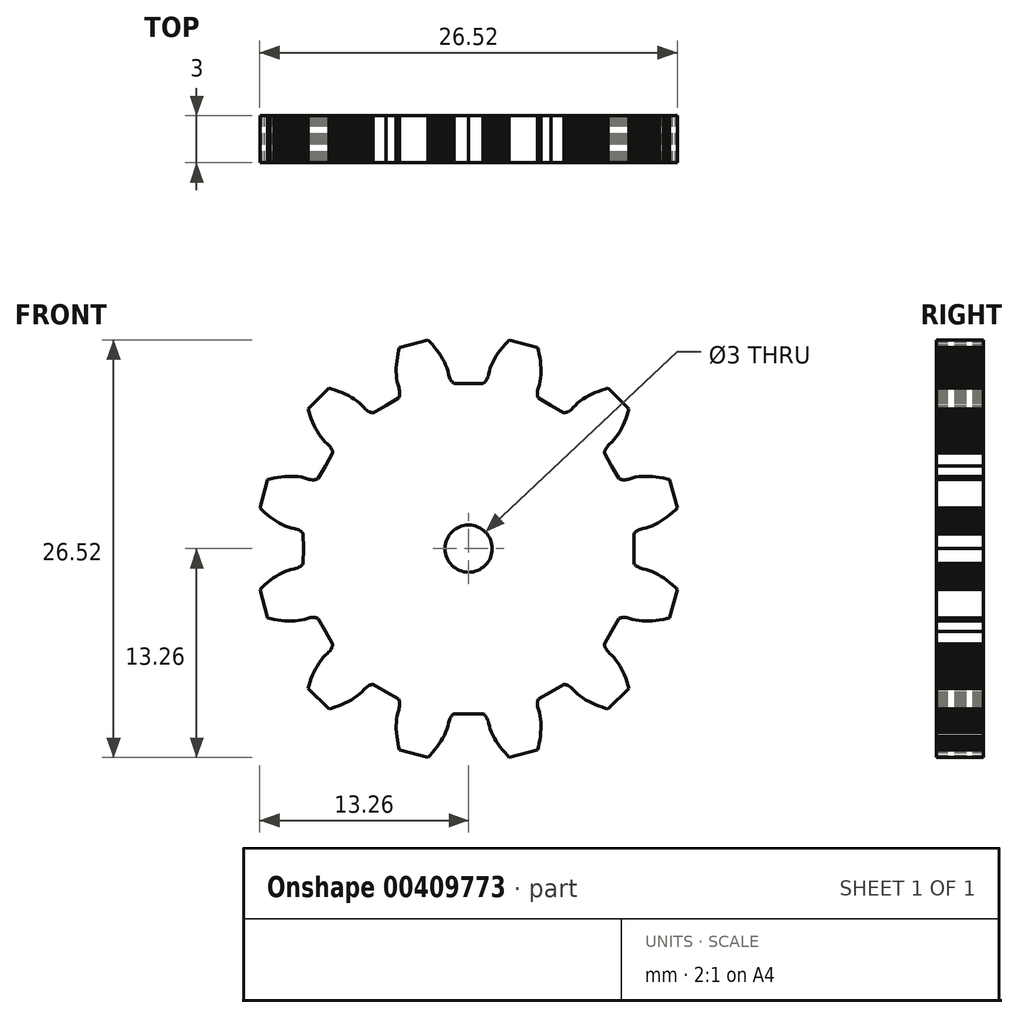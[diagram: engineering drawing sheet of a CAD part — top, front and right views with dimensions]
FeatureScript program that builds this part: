
annotation { "Feature Type Name" : "Feature", "Feature Type Description" : "" }
export const myFeature = defineFeature(function(context is Context, id is Id, definition is map)
    precondition{}
    {
        {
            var Q0;
            Q0=qCreatedBy(makeId("Front.planeOp"),FACE);
            var sketch = newSketch(context, id + "F0", { "sketchPlane" : qUnion([Q0])});
            skLineSegment(sketch, "E0", {"start": v(-10.5, 0) * mm, "end": v(-10.5, 0.93) * mm});
            skLineSegment(sketch, "E1", {"start": v(-10.5, 0.93) * mm, "end": v(-10.55, 1) * mm});
            skLineSegment(sketch, "E2", {"start": v(-10.55, 1) * mm, "end": v(-10.6, 1.05) * mm});
            skLineSegment(sketch, "E3", {"start": v(-10.6, 1.05) * mm, "end": v(-10.64, 1.09) * mm});
            skLineSegment(sketch, "E4", {"start": v(-10.64, 1.09) * mm, "end": v(-10.69, 1.12) * mm});
            skLineSegment(sketch, "E5", {"start": v(-10.69, 1.12) * mm, "end": v(-10.78, 1.17) * mm});
            skLineSegment(sketch, "E6", {"start": v(-10.78, 1.17) * mm, "end": v(-10.88, 1.22) * mm});
            skLineSegment(sketch, "E7", {"start": v(-10.88, 1.22) * mm, "end": v(-10.97, 1.25) * mm});
            skLineSegment(sketch, "E8", {"start": v(-10.97, 1.25) * mm, "end": v(-11.07, 1.28) * mm});
            skLineSegment(sketch, "E9", {"start": v(-11.07, 1.28) * mm, "end": v(-11.27, 1.32) * mm});
            skLineSegment(sketch, "E10", {"start": v(-11.27, 1.32) * mm, "end": v(-11.47, 1.38) * mm});
            skLineSegment(sketch, "E11", {"start": v(-11.47, 1.38) * mm, "end": v(-11.66, 1.45) * mm});
            skLineSegment(sketch, "E12", {"start": v(-11.66, 1.45) * mm, "end": v(-11.85, 1.54) * mm});
            skLineSegment(sketch, "E13", {"start": v(-11.85, 1.54) * mm, "end": v(-12.04, 1.64) * mm});
            skLineSegment(sketch, "E14", {"start": v(-12.04, 1.64) * mm, "end": v(-12.23, 1.76) * mm});
            skLineSegment(sketch, "E15", {"start": v(-12.23, 1.76) * mm, "end": v(-12.41, 1.88) * mm});
            skLineSegment(sketch, "E16", {"start": v(-12.41, 1.88) * mm, "end": v(-12.6, 2.01) * mm});
            skLineSegment(sketch, "E17", {"start": v(-12.6, 2.01) * mm, "end": v(-12.77, 2.15) * mm});
            skLineSegment(sketch, "E18", {"start": v(-12.77, 2.15) * mm, "end": v(-12.95, 2.3) * mm});
            skLineSegment(sketch, "E19", {"start": v(-12.95, 2.3) * mm, "end": v(-13.13, 2.46) * mm});
            skLineSegment(sketch, "E20", {"start": v(-13.13, 2.46) * mm, "end": v(-13.26, 2.58) * mm});
            skLineSegment(sketch, "E21", {"start": v(-13.26, 2.58) * mm, "end": v(-12.77, 4.4) * mm});
            skLineSegment(sketch, "E22", {"start": v(-12.77, 4.4) * mm, "end": v(-12.6, 4.43) * mm});
            skLineSegment(sketch, "E23", {"start": v(-12.6, 4.43) * mm, "end": v(-12.37, 4.48) * mm});
            skLineSegment(sketch, "E24", {"start": v(-12.37, 4.48) * mm, "end": v(-12.14, 4.52) * mm});
            skLineSegment(sketch, "E25", {"start": v(-12.14, 4.52) * mm, "end": v(-11.91, 4.56) * mm});
            skLineSegment(sketch, "E26", {"start": v(-11.91, 4.56) * mm, "end": v(-11.69, 4.58) * mm});
            skLineSegment(sketch, "E27", {"start": v(-11.69, 4.58) * mm, "end": v(-11.47, 4.6) * mm});
            skLineSegment(sketch, "E28", {"start": v(-11.47, 4.6) * mm, "end": v(-11.25, 4.6) * mm});
            skLineSegment(sketch, "E29", {"start": v(-11.25, 4.6) * mm, "end": v(-11.03, 4.59) * mm});
            skLineSegment(sketch, "E30", {"start": v(-11.03, 4.59) * mm, "end": v(-10.82, 4.57) * mm});
            skLineSegment(sketch, "E31", {"start": v(-10.82, 4.57) * mm, "end": v(-10.62, 4.54) * mm});
            skLineSegment(sketch, "E32", {"start": v(-10.62, 4.54) * mm, "end": v(-10.42, 4.5) * mm});
            skLineSegment(sketch, "E33", {"start": v(-10.42, 4.5) * mm, "end": v(-10.23, 4.43) * mm});
            skLineSegment(sketch, "E34", {"start": v(-10.23, 4.43) * mm, "end": v(-10.13, 4.4) * mm});
            skLineSegment(sketch, "E35", {"start": v(-10.13, 4.4) * mm, "end": v(-10.03, 4.38) * mm});
            skLineSegment(sketch, "E36", {"start": v(-10.03, 4.38) * mm, "end": v(-9.92, 4.37) * mm});
            skLineSegment(sketch, "E37", {"start": v(-9.92, 4.37) * mm, "end": v(-9.81, 4.37) * mm});
            skLineSegment(sketch, "E38", {"start": v(-9.81, 4.37) * mm, "end": v(-9.76, 4.38) * mm});
            skLineSegment(sketch, "E39", {"start": v(-9.76, 4.38) * mm, "end": v(-9.7, 4.39) * mm});
            skLineSegment(sketch, "E40", {"start": v(-9.7, 4.39) * mm, "end": v(-9.63, 4.4) * mm});
            skLineSegment(sketch, "E41", {"start": v(-9.63, 4.4) * mm, "end": v(-9.56, 4.44) * mm});
            skLineSegment(sketch, "E42", {"start": v(-9.56, 4.44) * mm, "end": v(-9.09, 5.25) * mm});
            skLineSegment(sketch, "E43", {"start": v(-9.09, 5.25) * mm, "end": v(-8.63, 6.06) * mm});
            skLineSegment(sketch, "E44", {"start": v(-8.63, 6.06) * mm, "end": v(-8.63, 6.14) * mm});
            skLineSegment(sketch, "E45", {"start": v(-8.63, 6.14) * mm, "end": v(-8.65, 6.2) * mm});
            skLineSegment(sketch, "E46", {"start": v(-8.65, 6.2) * mm, "end": v(-8.67, 6.26) * mm});
            skLineSegment(sketch, "E47", {"start": v(-8.67, 6.26) * mm, "end": v(-8.7, 6.31) * mm});
            skLineSegment(sketch, "E48", {"start": v(-8.7, 6.31) * mm, "end": v(-8.75, 6.4) * mm});
            skLineSegment(sketch, "E49", {"start": v(-8.75, 6.4) * mm, "end": v(-8.81, 6.5) * mm});
            skLineSegment(sketch, "E50", {"start": v(-8.81, 6.5) * mm, "end": v(-8.88, 6.57) * mm});
            skLineSegment(sketch, "E51", {"start": v(-8.88, 6.57) * mm, "end": v(-8.95, 6.64) * mm});
            skLineSegment(sketch, "E52", {"start": v(-8.95, 6.64) * mm, "end": v(-9.1, 6.78) * mm});
            skLineSegment(sketch, "E53", {"start": v(-9.1, 6.78) * mm, "end": v(-9.24, 6.92) * mm});
            skLineSegment(sketch, "E54", {"start": v(-9.24, 6.92) * mm, "end": v(-9.37, 7.09) * mm});
            skLineSegment(sketch, "E55", {"start": v(-9.37, 7.09) * mm, "end": v(-9.5, 7.26) * mm});
            skLineSegment(sketch, "E56", {"start": v(-9.5, 7.26) * mm, "end": v(-9.6, 7.44) * mm});
            skLineSegment(sketch, "E57", {"start": v(-9.6, 7.44) * mm, "end": v(-9.71, 7.63) * mm});
            skLineSegment(sketch, "E58", {"start": v(-9.71, 7.63) * mm, "end": v(-9.8, 7.83) * mm});
            skLineSegment(sketch, "E59", {"start": v(-9.8, 7.83) * mm, "end": v(-9.9, 8.04) * mm});
            skLineSegment(sketch, "E60", {"start": v(-9.9, 8.04) * mm, "end": v(-9.99, 8.25) * mm});
            skLineSegment(sketch, "E61", {"start": v(-9.99, 8.25) * mm, "end": v(-10.07, 8.47) * mm});
            skLineSegment(sketch, "E62", {"start": v(-10.07, 8.47) * mm, "end": v(-10.14, 8.7) * mm});
            skLineSegment(sketch, "E63", {"start": v(-10.14, 8.7) * mm, "end": v(-10.2, 8.87) * mm});
            skLineSegment(sketch, "E64", {"start": v(-10.2, 8.87) * mm, "end": v(-8.87, 10.2) * mm});
            skLineSegment(sketch, "E65", {"start": v(-8.87, 10.2) * mm, "end": v(-8.7, 10.14) * mm});
            skLineSegment(sketch, "E66", {"start": v(-8.7, 10.14) * mm, "end": v(-8.47, 10.07) * mm});
            skLineSegment(sketch, "E67", {"start": v(-8.47, 10.07) * mm, "end": v(-8.25, 9.99) * mm});
            skLineSegment(sketch, "E68", {"start": v(-8.25, 9.99) * mm, "end": v(-8.04, 9.9) * mm});
            skLineSegment(sketch, "E69", {"start": v(-8.04, 9.9) * mm, "end": v(-7.83, 9.8) * mm});
            skLineSegment(sketch, "E70", {"start": v(-7.83, 9.8) * mm, "end": v(-7.63, 9.71) * mm});
            skLineSegment(sketch, "E71", {"start": v(-7.63, 9.71) * mm, "end": v(-7.44, 9.6) * mm});
            skLineSegment(sketch, "E72", {"start": v(-7.44, 9.6) * mm, "end": v(-7.26, 9.5) * mm});
            skLineSegment(sketch, "E73", {"start": v(-7.26, 9.5) * mm, "end": v(-7.09, 9.37) * mm});
            skLineSegment(sketch, "E74", {"start": v(-7.09, 9.37) * mm, "end": v(-6.92, 9.24) * mm});
            skLineSegment(sketch, "E75", {"start": v(-6.92, 9.24) * mm, "end": v(-6.78, 9.1) * mm});
            skLineSegment(sketch, "E76", {"start": v(-6.78, 9.1) * mm, "end": v(-6.64, 8.95) * mm});
            skLineSegment(sketch, "E77", {"start": v(-6.64, 8.95) * mm, "end": v(-6.57, 8.88) * mm});
            skLineSegment(sketch, "E78", {"start": v(-6.57, 8.88) * mm, "end": v(-6.5, 8.81) * mm});
            skLineSegment(sketch, "E79", {"start": v(-6.5, 8.81) * mm, "end": v(-6.4, 8.75) * mm});
            skLineSegment(sketch, "E80", {"start": v(-6.4, 8.75) * mm, "end": v(-6.31, 8.7) * mm});
            skLineSegment(sketch, "E81", {"start": v(-6.31, 8.7) * mm, "end": v(-6.26, 8.67) * mm});
            skLineSegment(sketch, "E82", {"start": v(-6.26, 8.67) * mm, "end": v(-6.2, 8.65) * mm});
            skLineSegment(sketch, "E83", {"start": v(-6.2, 8.65) * mm, "end": v(-6.14, 8.63) * mm});
            skLineSegment(sketch, "E84", {"start": v(-6.14, 8.63) * mm, "end": v(-6.06, 8.63) * mm});
            skLineSegment(sketch, "E85", {"start": v(-6.06, 8.63) * mm, "end": v(-5.25, 9.09) * mm});
            skLineSegment(sketch, "E86", {"start": v(-5.25, 9.09) * mm, "end": v(-4.44, 9.56) * mm});
            skLineSegment(sketch, "E87", {"start": v(-4.44, 9.56) * mm, "end": v(-4.4, 9.63) * mm});
            skLineSegment(sketch, "E88", {"start": v(-4.4, 9.63) * mm, "end": v(-4.39, 9.7) * mm});
            skLineSegment(sketch, "E89", {"start": v(-4.39, 9.7) * mm, "end": v(-4.38, 9.76) * mm});
            skLineSegment(sketch, "E90", {"start": v(-4.38, 9.76) * mm, "end": v(-4.37, 9.81) * mm});
            skLineSegment(sketch, "E91", {"start": v(-4.37, 9.81) * mm, "end": v(-4.37, 9.92) * mm});
            skLineSegment(sketch, "E92", {"start": v(-4.37, 9.92) * mm, "end": v(-4.38, 10.03) * mm});
            skLineSegment(sketch, "E93", {"start": v(-4.38, 10.03) * mm, "end": v(-4.4, 10.13) * mm});
            skLineSegment(sketch, "E94", {"start": v(-4.4, 10.13) * mm, "end": v(-4.43, 10.23) * mm});
            skLineSegment(sketch, "E95", {"start": v(-4.43, 10.23) * mm, "end": v(-4.5, 10.42) * mm});
            skLineSegment(sketch, "E96", {"start": v(-4.5, 10.42) * mm, "end": v(-4.54, 10.62) * mm});
            skLineSegment(sketch, "E97", {"start": v(-4.54, 10.62) * mm, "end": v(-4.57, 10.82) * mm});
            skLineSegment(sketch, "E98", {"start": v(-4.57, 10.82) * mm, "end": v(-4.59, 11.03) * mm});
            skLineSegment(sketch, "E99", {"start": v(-4.59, 11.03) * mm, "end": v(-4.6, 11.25) * mm});
            skLineSegment(sketch, "E100", {"start": v(-4.6, 11.25) * mm, "end": v(-4.6, 11.47) * mm});
            skLineSegment(sketch, "E101", {"start": v(-4.6, 11.47) * mm, "end": v(-4.58, 11.69) * mm});
            skLineSegment(sketch, "E102", {"start": v(-4.58, 11.69) * mm, "end": v(-4.56, 11.91) * mm});
            skLineSegment(sketch, "E103", {"start": v(-4.56, 11.91) * mm, "end": v(-4.52, 12.14) * mm});
            skLineSegment(sketch, "E104", {"start": v(-4.52, 12.14) * mm, "end": v(-4.48, 12.37) * mm});
            skLineSegment(sketch, "E105", {"start": v(-4.48, 12.37) * mm, "end": v(-4.43, 12.6) * mm});
            skLineSegment(sketch, "E106", {"start": v(-4.43, 12.6) * mm, "end": v(-4.4, 12.77) * mm});
            skLineSegment(sketch, "E107", {"start": v(-4.4, 12.77) * mm, "end": v(-2.58, 13.26) * mm});
            skLineSegment(sketch, "E108", {"start": v(-2.58, 13.26) * mm, "end": v(-2.46, 13.13) * mm});
            skLineSegment(sketch, "E109", {"start": v(-2.46, 13.13) * mm, "end": v(-2.3, 12.95) * mm});
            skLineSegment(sketch, "E110", {"start": v(-2.3, 12.95) * mm, "end": v(-2.15, 12.77) * mm});
            skLineSegment(sketch, "E111", {"start": v(-2.15, 12.77) * mm, "end": v(-2.01, 12.6) * mm});
            skLineSegment(sketch, "E112", {"start": v(-2.01, 12.6) * mm, "end": v(-1.88, 12.41) * mm});
            skLineSegment(sketch, "E113", {"start": v(-1.88, 12.41) * mm, "end": v(-1.76, 12.23) * mm});
            skLineSegment(sketch, "E114", {"start": v(-1.76, 12.23) * mm, "end": v(-1.64, 12.04) * mm});
            skLineSegment(sketch, "E115", {"start": v(-1.64, 12.04) * mm, "end": v(-1.54, 11.85) * mm});
            skLineSegment(sketch, "E116", {"start": v(-1.54, 11.85) * mm, "end": v(-1.45, 11.66) * mm});
            skLineSegment(sketch, "E117", {"start": v(-1.45, 11.66) * mm, "end": v(-1.38, 11.47) * mm});
            skLineSegment(sketch, "E118", {"start": v(-1.38, 11.47) * mm, "end": v(-1.32, 11.27) * mm});
            skLineSegment(sketch, "E119", {"start": v(-1.32, 11.27) * mm, "end": v(-1.28, 11.07) * mm});
            skLineSegment(sketch, "E120", {"start": v(-1.28, 11.07) * mm, "end": v(-1.25, 10.97) * mm});
            skLineSegment(sketch, "E121", {"start": v(-1.25, 10.97) * mm, "end": v(-1.22, 10.88) * mm});
            skLineSegment(sketch, "E122", {"start": v(-1.22, 10.88) * mm, "end": v(-1.17, 10.78) * mm});
            skLineSegment(sketch, "E123", {"start": v(-1.17, 10.78) * mm, "end": v(-1.12, 10.69) * mm});
            skLineSegment(sketch, "E124", {"start": v(-1.12, 10.69) * mm, "end": v(-1.09, 10.64) * mm});
            skLineSegment(sketch, "E125", {"start": v(-1.09, 10.64) * mm, "end": v(-1.05, 10.6) * mm});
            skLineSegment(sketch, "E126", {"start": v(-1.05, 10.6) * mm, "end": v(-1, 10.55) * mm});
            skLineSegment(sketch, "E127", {"start": v(-1, 10.55) * mm, "end": v(-0.93, 10.5) * mm});
            skLineSegment(sketch, "E128", {"start": v(-0.93, 10.5) * mm, "end": v(0, 10.5) * mm});
            skLineSegment(sketch, "E129", {"start": v(0, 10.5) * mm, "end": v(0.93, 10.5) * mm});
            skLineSegment(sketch, "E130", {"start": v(0.93, 10.5) * mm, "end": v(1, 10.55) * mm});
            skLineSegment(sketch, "E131", {"start": v(1, 10.55) * mm, "end": v(1.05, 10.6) * mm});
            skLineSegment(sketch, "E132", {"start": v(1.05, 10.6) * mm, "end": v(1.09, 10.64) * mm});
            skLineSegment(sketch, "E133", {"start": v(1.09, 10.64) * mm, "end": v(1.12, 10.69) * mm});
            skLineSegment(sketch, "E134", {"start": v(1.12, 10.69) * mm, "end": v(1.17, 10.78) * mm});
            skLineSegment(sketch, "E135", {"start": v(1.17, 10.78) * mm, "end": v(1.22, 10.88) * mm});
            skLineSegment(sketch, "E136", {"start": v(1.22, 10.88) * mm, "end": v(1.25, 10.97) * mm});
            skLineSegment(sketch, "E137", {"start": v(1.25, 10.97) * mm, "end": v(1.28, 11.07) * mm});
            skLineSegment(sketch, "E138", {"start": v(1.28, 11.07) * mm, "end": v(1.32, 11.27) * mm});
            skLineSegment(sketch, "E139", {"start": v(1.32, 11.27) * mm, "end": v(1.38, 11.47) * mm});
            skLineSegment(sketch, "E140", {"start": v(1.38, 11.47) * mm, "end": v(1.45, 11.66) * mm});
            skLineSegment(sketch, "E141", {"start": v(1.45, 11.66) * mm, "end": v(1.54, 11.85) * mm});
            skLineSegment(sketch, "E142", {"start": v(1.54, 11.85) * mm, "end": v(1.64, 12.04) * mm});
            skLineSegment(sketch, "E143", {"start": v(1.64, 12.04) * mm, "end": v(1.76, 12.23) * mm});
            skLineSegment(sketch, "E144", {"start": v(1.76, 12.23) * mm, "end": v(1.88, 12.41) * mm});
            skLineSegment(sketch, "E145", {"start": v(1.88, 12.41) * mm, "end": v(2.01, 12.6) * mm});
            skLineSegment(sketch, "E146", {"start": v(2.01, 12.6) * mm, "end": v(2.15, 12.77) * mm});
            skLineSegment(sketch, "E147", {"start": v(2.15, 12.77) * mm, "end": v(2.3, 12.95) * mm});
            skLineSegment(sketch, "E148", {"start": v(2.3, 12.95) * mm, "end": v(2.46, 13.13) * mm});
            skLineSegment(sketch, "E149", {"start": v(2.46, 13.13) * mm, "end": v(2.58, 13.26) * mm});
            skLineSegment(sketch, "E150", {"start": v(2.58, 13.26) * mm, "end": v(4.4, 12.77) * mm});
            skLineSegment(sketch, "E151", {"start": v(4.4, 12.77) * mm, "end": v(4.43, 12.6) * mm});
            skLineSegment(sketch, "E152", {"start": v(4.43, 12.6) * mm, "end": v(4.48, 12.37) * mm});
            skLineSegment(sketch, "E153", {"start": v(4.48, 12.37) * mm, "end": v(4.52, 12.14) * mm});
            skLineSegment(sketch, "E154", {"start": v(4.52, 12.14) * mm, "end": v(4.56, 11.91) * mm});
            skLineSegment(sketch, "E155", {"start": v(4.56, 11.91) * mm, "end": v(4.58, 11.69) * mm});
            skLineSegment(sketch, "E156", {"start": v(4.58, 11.69) * mm, "end": v(4.6, 11.47) * mm});
            skLineSegment(sketch, "E157", {"start": v(4.6, 11.47) * mm, "end": v(4.6, 11.25) * mm});
            skLineSegment(sketch, "E158", {"start": v(4.6, 11.25) * mm, "end": v(4.59, 11.03) * mm});
            skLineSegment(sketch, "E159", {"start": v(4.59, 11.03) * mm, "end": v(4.57, 10.82) * mm});
            skLineSegment(sketch, "E160", {"start": v(4.57, 10.82) * mm, "end": v(4.54, 10.62) * mm});
            skLineSegment(sketch, "E161", {"start": v(4.54, 10.62) * mm, "end": v(4.5, 10.42) * mm});
            skLineSegment(sketch, "E162", {"start": v(4.5, 10.42) * mm, "end": v(4.43, 10.23) * mm});
            skLineSegment(sketch, "E163", {"start": v(4.43, 10.23) * mm, "end": v(4.4, 10.13) * mm});
            skLineSegment(sketch, "E164", {"start": v(4.4, 10.13) * mm, "end": v(4.38, 10.03) * mm});
            skLineSegment(sketch, "E165", {"start": v(4.38, 10.03) * mm, "end": v(4.37, 9.92) * mm});
            skLineSegment(sketch, "E166", {"start": v(4.37, 9.92) * mm, "end": v(4.37, 9.81) * mm});
            skLineSegment(sketch, "E167", {"start": v(4.37, 9.81) * mm, "end": v(4.38, 9.76) * mm});
            skLineSegment(sketch, "E168", {"start": v(4.38, 9.76) * mm, "end": v(4.39, 9.7) * mm});
            skLineSegment(sketch, "E169", {"start": v(4.39, 9.7) * mm, "end": v(4.4, 9.63) * mm});
            skLineSegment(sketch, "E170", {"start": v(4.4, 9.63) * mm, "end": v(4.44, 9.56) * mm});
            skLineSegment(sketch, "E171", {"start": v(4.44, 9.56) * mm, "end": v(5.25, 9.09) * mm});
            skLineSegment(sketch, "E172", {"start": v(5.25, 9.09) * mm, "end": v(6.06, 8.63) * mm});
            skLineSegment(sketch, "E173", {"start": v(6.06, 8.63) * mm, "end": v(6.14, 8.63) * mm});
            skLineSegment(sketch, "E174", {"start": v(6.14, 8.63) * mm, "end": v(6.2, 8.65) * mm});
            skLineSegment(sketch, "E175", {"start": v(6.2, 8.65) * mm, "end": v(6.26, 8.67) * mm});
            skLineSegment(sketch, "E176", {"start": v(6.26, 8.67) * mm, "end": v(6.31, 8.7) * mm});
            skLineSegment(sketch, "E177", {"start": v(6.31, 8.7) * mm, "end": v(6.4, 8.75) * mm});
            skLineSegment(sketch, "E178", {"start": v(6.4, 8.75) * mm, "end": v(6.5, 8.81) * mm});
            skLineSegment(sketch, "E179", {"start": v(6.5, 8.81) * mm, "end": v(6.57, 8.88) * mm});
            skLineSegment(sketch, "E180", {"start": v(6.57, 8.88) * mm, "end": v(6.64, 8.95) * mm});
            skLineSegment(sketch, "E181", {"start": v(6.64, 8.95) * mm, "end": v(6.78, 9.1) * mm});
            skLineSegment(sketch, "E182", {"start": v(6.78, 9.1) * mm, "end": v(6.92, 9.24) * mm});
            skLineSegment(sketch, "E183", {"start": v(6.92, 9.24) * mm, "end": v(7.09, 9.37) * mm});
            skLineSegment(sketch, "E184", {"start": v(7.09, 9.37) * mm, "end": v(7.26, 9.5) * mm});
            skLineSegment(sketch, "E185", {"start": v(7.26, 9.5) * mm, "end": v(7.44, 9.6) * mm});
            skLineSegment(sketch, "E186", {"start": v(7.44, 9.6) * mm, "end": v(7.63, 9.71) * mm});
            skLineSegment(sketch, "E187", {"start": v(7.63, 9.71) * mm, "end": v(7.83, 9.8) * mm});
            skLineSegment(sketch, "E188", {"start": v(7.83, 9.8) * mm, "end": v(8.04, 9.9) * mm});
            skLineSegment(sketch, "E189", {"start": v(8.04, 9.9) * mm, "end": v(8.25, 9.99) * mm});
            skLineSegment(sketch, "E190", {"start": v(8.25, 9.99) * mm, "end": v(8.47, 10.07) * mm});
            skLineSegment(sketch, "E191", {"start": v(8.47, 10.07) * mm, "end": v(8.7, 10.14) * mm});
            skLineSegment(sketch, "E192", {"start": v(8.7, 10.14) * mm, "end": v(8.87, 10.2) * mm});
            skLineSegment(sketch, "E193", {"start": v(8.87, 10.2) * mm, "end": v(10.19, 8.87) * mm});
            skLineSegment(sketch, "E194", {"start": v(10.19, 8.87) * mm, "end": v(10.14, 8.7) * mm});
            skLineSegment(sketch, "E195", {"start": v(10.14, 8.7) * mm, "end": v(10.07, 8.47) * mm});
            skLineSegment(sketch, "E196", {"start": v(10.07, 8.47) * mm, "end": v(9.99, 8.25) * mm});
            skLineSegment(sketch, "E197", {"start": v(9.99, 8.25) * mm, "end": v(9.9, 8.04) * mm});
            skLineSegment(sketch, "E198", {"start": v(9.9, 8.04) * mm, "end": v(9.8, 7.83) * mm});
            skLineSegment(sketch, "E199", {"start": v(9.8, 7.83) * mm, "end": v(9.71, 7.63) * mm});
            skLineSegment(sketch, "E200", {"start": v(9.71, 7.63) * mm, "end": v(9.6, 7.44) * mm});
            skLineSegment(sketch, "E201", {"start": v(9.6, 7.44) * mm, "end": v(9.5, 7.26) * mm});
            skLineSegment(sketch, "E202", {"start": v(9.5, 7.26) * mm, "end": v(9.37, 7.09) * mm});
            skLineSegment(sketch, "E203", {"start": v(9.37, 7.09) * mm, "end": v(9.24, 6.92) * mm});
            skLineSegment(sketch, "E204", {"start": v(9.24, 6.92) * mm, "end": v(9.1, 6.78) * mm});
            skLineSegment(sketch, "E205", {"start": v(9.1, 6.78) * mm, "end": v(8.95, 6.64) * mm});
            skLineSegment(sketch, "E206", {"start": v(8.95, 6.64) * mm, "end": v(8.88, 6.57) * mm});
            skLineSegment(sketch, "E207", {"start": v(8.88, 6.57) * mm, "end": v(8.81, 6.5) * mm});
            skLineSegment(sketch, "E208", {"start": v(8.81, 6.5) * mm, "end": v(8.75, 6.4) * mm});
            skLineSegment(sketch, "E209", {"start": v(8.75, 6.4) * mm, "end": v(8.7, 6.31) * mm});
            skLineSegment(sketch, "E210", {"start": v(8.7, 6.31) * mm, "end": v(8.67, 6.26) * mm});
            skLineSegment(sketch, "E211", {"start": v(8.67, 6.26) * mm, "end": v(8.65, 6.2) * mm});
            skLineSegment(sketch, "E212", {"start": v(8.65, 6.2) * mm, "end": v(8.63, 6.14) * mm});
            skLineSegment(sketch, "E213", {"start": v(8.63, 6.14) * mm, "end": v(8.63, 6.06) * mm});
            skLineSegment(sketch, "E214", {"start": v(8.63, 6.06) * mm, "end": v(9.09, 5.25) * mm});
            skLineSegment(sketch, "E215", {"start": v(9.09, 5.25) * mm, "end": v(9.56, 4.44) * mm});
            skLineSegment(sketch, "E216", {"start": v(9.56, 4.44) * mm, "end": v(9.63, 4.4) * mm});
            skLineSegment(sketch, "E217", {"start": v(9.63, 4.4) * mm, "end": v(9.7, 4.39) * mm});
            skLineSegment(sketch, "E218", {"start": v(9.7, 4.39) * mm, "end": v(9.76, 4.38) * mm});
            skLineSegment(sketch, "E219", {"start": v(9.76, 4.38) * mm, "end": v(9.81, 4.37) * mm});
            skLineSegment(sketch, "E220", {"start": v(9.81, 4.37) * mm, "end": v(9.92, 4.37) * mm});
            skLineSegment(sketch, "E221", {"start": v(9.92, 4.37) * mm, "end": v(10.03, 4.38) * mm});
            skLineSegment(sketch, "E222", {"start": v(10.03, 4.38) * mm, "end": v(10.13, 4.4) * mm});
            skLineSegment(sketch, "E223", {"start": v(10.13, 4.4) * mm, "end": v(10.23, 4.43) * mm});
            skLineSegment(sketch, "E224", {"start": v(10.23, 4.43) * mm, "end": v(10.42, 4.5) * mm});
            skLineSegment(sketch, "E225", {"start": v(10.42, 4.5) * mm, "end": v(10.62, 4.54) * mm});
            skLineSegment(sketch, "E226", {"start": v(10.62, 4.54) * mm, "end": v(10.82, 4.57) * mm});
            skLineSegment(sketch, "E227", {"start": v(10.82, 4.57) * mm, "end": v(11.03, 4.59) * mm});
            skLineSegment(sketch, "E228", {"start": v(11.03, 4.59) * mm, "end": v(11.25, 4.6) * mm});
            skLineSegment(sketch, "E229", {"start": v(11.25, 4.6) * mm, "end": v(11.47, 4.6) * mm});
            skLineSegment(sketch, "E230", {"start": v(11.47, 4.6) * mm, "end": v(11.69, 4.58) * mm});
            skLineSegment(sketch, "E231", {"start": v(11.69, 4.58) * mm, "end": v(11.91, 4.56) * mm});
            skLineSegment(sketch, "E232", {"start": v(11.91, 4.56) * mm, "end": v(12.14, 4.52) * mm});
            skLineSegment(sketch, "E233", {"start": v(12.14, 4.52) * mm, "end": v(12.37, 4.48) * mm});
            skLineSegment(sketch, "E234", {"start": v(12.37, 4.48) * mm, "end": v(12.6, 4.43) * mm});
            skLineSegment(sketch, "E235", {"start": v(12.6, 4.43) * mm, "end": v(12.77, 4.4) * mm});
            skLineSegment(sketch, "E236", {"start": v(12.77, 4.4) * mm, "end": v(13.26, 2.58) * mm});
            skLineSegment(sketch, "E237", {"start": v(13.26, 2.58) * mm, "end": v(13.13, 2.46) * mm});
            skLineSegment(sketch, "E238", {"start": v(13.13, 2.46) * mm, "end": v(12.95, 2.3) * mm});
            skLineSegment(sketch, "E239", {"start": v(12.95, 2.3) * mm, "end": v(12.77, 2.15) * mm});
            skLineSegment(sketch, "E240", {"start": v(12.77, 2.15) * mm, "end": v(12.6, 2.01) * mm});
            skLineSegment(sketch, "E241", {"start": v(12.6, 2.01) * mm, "end": v(12.41, 1.88) * mm});
            skLineSegment(sketch, "E242", {"start": v(12.41, 1.88) * mm, "end": v(12.23, 1.76) * mm});
            skLineSegment(sketch, "E243", {"start": v(12.23, 1.76) * mm, "end": v(12.04, 1.64) * mm});
            skLineSegment(sketch, "E244", {"start": v(12.04, 1.64) * mm, "end": v(11.85, 1.54) * mm});
            skLineSegment(sketch, "E245", {"start": v(11.85, 1.54) * mm, "end": v(11.66, 1.45) * mm});
            skLineSegment(sketch, "E246", {"start": v(11.66, 1.45) * mm, "end": v(11.47, 1.38) * mm});
            skLineSegment(sketch, "E247", {"start": v(11.47, 1.38) * mm, "end": v(11.27, 1.32) * mm});
            skLineSegment(sketch, "E248", {"start": v(11.27, 1.32) * mm, "end": v(11.07, 1.28) * mm});
            skLineSegment(sketch, "E249", {"start": v(11.07, 1.28) * mm, "end": v(10.97, 1.25) * mm});
            skLineSegment(sketch, "E250", {"start": v(10.97, 1.25) * mm, "end": v(10.88, 1.22) * mm});
            skLineSegment(sketch, "E251", {"start": v(10.88, 1.22) * mm, "end": v(10.78, 1.17) * mm});
            skLineSegment(sketch, "E252", {"start": v(10.78, 1.17) * mm, "end": v(10.69, 1.12) * mm});
            skLineSegment(sketch, "E253", {"start": v(10.69, 1.12) * mm, "end": v(10.64, 1.09) * mm});
            skLineSegment(sketch, "E254", {"start": v(10.64, 1.09) * mm, "end": v(10.6, 1.05) * mm});
            skLineSegment(sketch, "E255", {"start": v(10.6, 1.05) * mm, "end": v(10.55, 1) * mm});
            skLineSegment(sketch, "E256", {"start": v(10.55, 1) * mm, "end": v(10.5, 0.93) * mm});
            skLineSegment(sketch, "E257", {"start": v(10.5, 0.93) * mm, "end": v(10.5, 0) * mm});
            skLineSegment(sketch, "E258", {"start": v(10.5, 0) * mm, "end": v(10.5, -0.93) * mm});
            skLineSegment(sketch, "E259", {"start": v(10.5, -0.93) * mm, "end": v(10.55, -1) * mm});
            skLineSegment(sketch, "E260", {"start": v(10.55, -1) * mm, "end": v(10.6, -1.05) * mm});
            skLineSegment(sketch, "E261", {"start": v(10.6, -1.05) * mm, "end": v(10.64, -1.09) * mm});
            skLineSegment(sketch, "E262", {"start": v(10.64, -1.09) * mm, "end": v(10.69, -1.12) * mm});
            skLineSegment(sketch, "E263", {"start": v(10.69, -1.12) * mm, "end": v(10.78, -1.17) * mm});
            skLineSegment(sketch, "E264", {"start": v(10.78, -1.17) * mm, "end": v(10.88, -1.22) * mm});
            skLineSegment(sketch, "E265", {"start": v(10.88, -1.22) * mm, "end": v(10.97, -1.25) * mm});
            skLineSegment(sketch, "E266", {"start": v(10.97, -1.25) * mm, "end": v(11.07, -1.28) * mm});
            skLineSegment(sketch, "E267", {"start": v(11.07, -1.28) * mm, "end": v(11.27, -1.32) * mm});
            skLineSegment(sketch, "E268", {"start": v(11.27, -1.32) * mm, "end": v(11.47, -1.38) * mm});
            skLineSegment(sketch, "E269", {"start": v(11.47, -1.38) * mm, "end": v(11.66, -1.45) * mm});
            skLineSegment(sketch, "E270", {"start": v(11.66, -1.45) * mm, "end": v(11.85, -1.54) * mm});
            skLineSegment(sketch, "E271", {"start": v(11.85, -1.54) * mm, "end": v(12.04, -1.64) * mm});
            skLineSegment(sketch, "E272", {"start": v(12.04, -1.64) * mm, "end": v(12.23, -1.76) * mm});
            skLineSegment(sketch, "E273", {"start": v(12.23, -1.76) * mm, "end": v(12.41, -1.88) * mm});
            skLineSegment(sketch, "E274", {"start": v(12.41, -1.88) * mm, "end": v(12.6, -2.01) * mm});
            skLineSegment(sketch, "E275", {"start": v(12.6, -2.01) * mm, "end": v(12.77, -2.15) * mm});
            skLineSegment(sketch, "E276", {"start": v(12.77, -2.15) * mm, "end": v(12.95, -2.3) * mm});
            skLineSegment(sketch, "E277", {"start": v(12.95, -2.3) * mm, "end": v(13.13, -2.46) * mm});
            skLineSegment(sketch, "E278", {"start": v(13.13, -2.46) * mm, "end": v(13.26, -2.58) * mm});
            skLineSegment(sketch, "E279", {"start": v(13.26, -2.58) * mm, "end": v(12.77, -4.4) * mm});
            skLineSegment(sketch, "E280", {"start": v(12.77, -4.4) * mm, "end": v(12.6, -4.43) * mm});
            skLineSegment(sketch, "E281", {"start": v(12.6, -4.43) * mm, "end": v(12.37, -4.48) * mm});
            skLineSegment(sketch, "E282", {"start": v(12.37, -4.48) * mm, "end": v(12.14, -4.52) * mm});
            skLineSegment(sketch, "E283", {"start": v(12.14, -4.52) * mm, "end": v(11.91, -4.56) * mm});
            skLineSegment(sketch, "E284", {"start": v(11.91, -4.56) * mm, "end": v(11.69, -4.58) * mm});
            skLineSegment(sketch, "E285", {"start": v(11.69, -4.58) * mm, "end": v(11.47, -4.6) * mm});
            skLineSegment(sketch, "E286", {"start": v(11.47, -4.6) * mm, "end": v(11.25, -4.6) * mm});
            skLineSegment(sketch, "E287", {"start": v(11.25, -4.6) * mm, "end": v(11.03, -4.59) * mm});
            skLineSegment(sketch, "E288", {"start": v(11.03, -4.59) * mm, "end": v(10.82, -4.57) * mm});
            skLineSegment(sketch, "E289", {"start": v(10.82, -4.57) * mm, "end": v(10.62, -4.54) * mm});
            skLineSegment(sketch, "E290", {"start": v(10.62, -4.54) * mm, "end": v(10.42, -4.5) * mm});
            skLineSegment(sketch, "E291", {"start": v(10.42, -4.5) * mm, "end": v(10.23, -4.43) * mm});
            skLineSegment(sketch, "E292", {"start": v(10.23, -4.43) * mm, "end": v(10.13, -4.4) * mm});
            skLineSegment(sketch, "E293", {"start": v(10.13, -4.4) * mm, "end": v(10.03, -4.38) * mm});
            skLineSegment(sketch, "E294", {"start": v(10.03, -4.38) * mm, "end": v(9.92, -4.37) * mm});
            skLineSegment(sketch, "E295", {"start": v(9.92, -4.37) * mm, "end": v(9.81, -4.37) * mm});
            skLineSegment(sketch, "E296", {"start": v(9.81, -4.37) * mm, "end": v(9.76, -4.38) * mm});
            skLineSegment(sketch, "E297", {"start": v(9.76, -4.38) * mm, "end": v(9.7, -4.39) * mm});
            skLineSegment(sketch, "E298", {"start": v(9.7, -4.39) * mm, "end": v(9.63, -4.4) * mm});
            skLineSegment(sketch, "E299", {"start": v(9.63, -4.4) * mm, "end": v(9.56, -4.44) * mm});
            skLineSegment(sketch, "E300", {"start": v(9.56, -4.44) * mm, "end": v(9.09, -5.25) * mm});
            skLineSegment(sketch, "E301", {"start": v(9.09, -5.25) * mm, "end": v(8.63, -6.06) * mm});
            skLineSegment(sketch, "E302", {"start": v(8.63, -6.06) * mm, "end": v(8.63, -6.14) * mm});
            skLineSegment(sketch, "E303", {"start": v(8.63, -6.14) * mm, "end": v(8.65, -6.2) * mm});
            skLineSegment(sketch, "E304", {"start": v(8.65, -6.2) * mm, "end": v(8.67, -6.26) * mm});
            skLineSegment(sketch, "E305", {"start": v(8.67, -6.26) * mm, "end": v(8.7, -6.31) * mm});
            skLineSegment(sketch, "E306", {"start": v(8.7, -6.31) * mm, "end": v(8.75, -6.4) * mm});
            skLineSegment(sketch, "E307", {"start": v(8.75, -6.4) * mm, "end": v(8.81, -6.5) * mm});
            skLineSegment(sketch, "E308", {"start": v(8.81, -6.5) * mm, "end": v(8.88, -6.57) * mm});
            skLineSegment(sketch, "E309", {"start": v(8.88, -6.57) * mm, "end": v(8.95, -6.64) * mm});
            skLineSegment(sketch, "E310", {"start": v(8.95, -6.64) * mm, "end": v(9.1, -6.78) * mm});
            skLineSegment(sketch, "E311", {"start": v(9.1, -6.78) * mm, "end": v(9.24, -6.92) * mm});
            skLineSegment(sketch, "E312", {"start": v(9.24, -6.92) * mm, "end": v(9.37, -7.09) * mm});
            skLineSegment(sketch, "E313", {"start": v(9.37, -7.09) * mm, "end": v(9.5, -7.26) * mm});
            skLineSegment(sketch, "E314", {"start": v(9.5, -7.26) * mm, "end": v(9.6, -7.44) * mm});
            skLineSegment(sketch, "E315", {"start": v(9.6, -7.44) * mm, "end": v(9.71, -7.63) * mm});
            skLineSegment(sketch, "E316", {"start": v(9.71, -7.63) * mm, "end": v(9.8, -7.83) * mm});
            skLineSegment(sketch, "E317", {"start": v(9.8, -7.83) * mm, "end": v(9.9, -8.04) * mm});
            skLineSegment(sketch, "E318", {"start": v(9.9, -8.04) * mm, "end": v(9.99, -8.25) * mm});
            skLineSegment(sketch, "E319", {"start": v(9.99, -8.25) * mm, "end": v(10.07, -8.47) * mm});
            skLineSegment(sketch, "E320", {"start": v(10.07, -8.47) * mm, "end": v(10.14, -8.7) * mm});
            skLineSegment(sketch, "E321", {"start": v(10.14, -8.7) * mm, "end": v(10.19, -8.87) * mm});
            skLineSegment(sketch, "E322", {"start": v(10.19, -8.87) * mm, "end": v(8.87, -10.19) * mm});
            skLineSegment(sketch, "E323", {"start": v(8.87, -10.19) * mm, "end": v(8.7, -10.14) * mm});
            skLineSegment(sketch, "E324", {"start": v(8.7, -10.14) * mm, "end": v(8.47, -10.07) * mm});
            skLineSegment(sketch, "E325", {"start": v(8.47, -10.07) * mm, "end": v(8.25, -9.99) * mm});
            skLineSegment(sketch, "E326", {"start": v(8.25, -9.99) * mm, "end": v(8.04, -9.9) * mm});
            skLineSegment(sketch, "E327", {"start": v(8.04, -9.9) * mm, "end": v(7.83, -9.8) * mm});
            skLineSegment(sketch, "E328", {"start": v(7.83, -9.8) * mm, "end": v(7.63, -9.71) * mm});
            skLineSegment(sketch, "E329", {"start": v(7.63, -9.71) * mm, "end": v(7.44, -9.6) * mm});
            skLineSegment(sketch, "E330", {"start": v(7.44, -9.6) * mm, "end": v(7.26, -9.5) * mm});
            skLineSegment(sketch, "E331", {"start": v(7.26, -9.5) * mm, "end": v(7.09, -9.37) * mm});
            skLineSegment(sketch, "E332", {"start": v(7.09, -9.37) * mm, "end": v(6.92, -9.24) * mm});
            skLineSegment(sketch, "E333", {"start": v(6.92, -9.24) * mm, "end": v(6.78, -9.1) * mm});
            skLineSegment(sketch, "E334", {"start": v(6.78, -9.1) * mm, "end": v(6.64, -8.95) * mm});
            skLineSegment(sketch, "E335", {"start": v(6.64, -8.95) * mm, "end": v(6.57, -8.88) * mm});
            skLineSegment(sketch, "E336", {"start": v(6.57, -8.88) * mm, "end": v(6.5, -8.81) * mm});
            skLineSegment(sketch, "E337", {"start": v(6.5, -8.81) * mm, "end": v(6.4, -8.75) * mm});
            skLineSegment(sketch, "E338", {"start": v(6.4, -8.75) * mm, "end": v(6.31, -8.7) * mm});
            skLineSegment(sketch, "E339", {"start": v(6.31, -8.7) * mm, "end": v(6.26, -8.67) * mm});
            skLineSegment(sketch, "E340", {"start": v(6.26, -8.67) * mm, "end": v(6.2, -8.65) * mm});
            skLineSegment(sketch, "E341", {"start": v(6.2, -8.65) * mm, "end": v(6.14, -8.63) * mm});
            skLineSegment(sketch, "E342", {"start": v(6.14, -8.63) * mm, "end": v(6.06, -8.63) * mm});
            skLineSegment(sketch, "E343", {"start": v(6.06, -8.63) * mm, "end": v(5.25, -9.09) * mm});
            skLineSegment(sketch, "E344", {"start": v(5.25, -9.09) * mm, "end": v(4.44, -9.56) * mm});
            skLineSegment(sketch, "E345", {"start": v(4.44, -9.56) * mm, "end": v(4.4, -9.63) * mm});
            skLineSegment(sketch, "E346", {"start": v(4.4, -9.63) * mm, "end": v(4.39, -9.7) * mm});
            skLineSegment(sketch, "E347", {"start": v(4.39, -9.7) * mm, "end": v(4.38, -9.76) * mm});
            skLineSegment(sketch, "E348", {"start": v(4.38, -9.76) * mm, "end": v(4.37, -9.81) * mm});
            skLineSegment(sketch, "E349", {"start": v(4.37, -9.81) * mm, "end": v(4.37, -9.92) * mm});
            skLineSegment(sketch, "E350", {"start": v(4.37, -9.92) * mm, "end": v(4.38, -10.03) * mm});
            skLineSegment(sketch, "E351", {"start": v(4.38, -10.03) * mm, "end": v(4.4, -10.13) * mm});
            skLineSegment(sketch, "E352", {"start": v(4.4, -10.13) * mm, "end": v(4.43, -10.23) * mm});
            skLineSegment(sketch, "E353", {"start": v(4.43, -10.23) * mm, "end": v(4.5, -10.42) * mm});
            skLineSegment(sketch, "E354", {"start": v(4.5, -10.42) * mm, "end": v(4.54, -10.62) * mm});
            skLineSegment(sketch, "E355", {"start": v(4.54, -10.62) * mm, "end": v(4.57, -10.82) * mm});
            skLineSegment(sketch, "E356", {"start": v(4.57, -10.82) * mm, "end": v(4.59, -11.03) * mm});
            skLineSegment(sketch, "E357", {"start": v(4.59, -11.03) * mm, "end": v(4.6, -11.25) * mm});
            skLineSegment(sketch, "E358", {"start": v(4.6, -11.25) * mm, "end": v(4.6, -11.47) * mm});
            skLineSegment(sketch, "E359", {"start": v(4.6, -11.47) * mm, "end": v(4.58, -11.69) * mm});
            skLineSegment(sketch, "E360", {"start": v(4.58, -11.69) * mm, "end": v(4.56, -11.91) * mm});
            skLineSegment(sketch, "E361", {"start": v(4.56, -11.91) * mm, "end": v(4.52, -12.14) * mm});
            skLineSegment(sketch, "E362", {"start": v(4.52, -12.14) * mm, "end": v(4.48, -12.37) * mm});
            skLineSegment(sketch, "E363", {"start": v(4.48, -12.37) * mm, "end": v(4.43, -12.6) * mm});
            skLineSegment(sketch, "E364", {"start": v(4.43, -12.6) * mm, "end": v(4.4, -12.77) * mm});
            skLineSegment(sketch, "E365", {"start": v(4.4, -12.77) * mm, "end": v(2.58, -13.26) * mm});
            skLineSegment(sketch, "E366", {"start": v(2.58, -13.26) * mm, "end": v(2.46, -13.13) * mm});
            skLineSegment(sketch, "E367", {"start": v(2.46, -13.13) * mm, "end": v(2.3, -12.95) * mm});
            skLineSegment(sketch, "E368", {"start": v(2.3, -12.95) * mm, "end": v(2.15, -12.77) * mm});
            skLineSegment(sketch, "E369", {"start": v(2.15, -12.77) * mm, "end": v(2.01, -12.6) * mm});
            skLineSegment(sketch, "E370", {"start": v(2.01, -12.6) * mm, "end": v(1.88, -12.41) * mm});
            skLineSegment(sketch, "E371", {"start": v(1.88, -12.41) * mm, "end": v(1.76, -12.23) * mm});
            skLineSegment(sketch, "E372", {"start": v(1.76, -12.23) * mm, "end": v(1.64, -12.04) * mm});
            skLineSegment(sketch, "E373", {"start": v(1.64, -12.04) * mm, "end": v(1.54, -11.85) * mm});
            skLineSegment(sketch, "E374", {"start": v(1.54, -11.85) * mm, "end": v(1.45, -11.66) * mm});
            skLineSegment(sketch, "E375", {"start": v(1.45, -11.66) * mm, "end": v(1.38, -11.47) * mm});
            skLineSegment(sketch, "E376", {"start": v(1.38, -11.47) * mm, "end": v(1.32, -11.27) * mm});
            skLineSegment(sketch, "E377", {"start": v(1.32, -11.27) * mm, "end": v(1.28, -11.07) * mm});
            skLineSegment(sketch, "E378", {"start": v(1.28, -11.07) * mm, "end": v(1.25, -10.97) * mm});
            skLineSegment(sketch, "E379", {"start": v(1.25, -10.97) * mm, "end": v(1.22, -10.88) * mm});
            skLineSegment(sketch, "E380", {"start": v(1.22, -10.88) * mm, "end": v(1.17, -10.78) * mm});
            skLineSegment(sketch, "E381", {"start": v(1.17, -10.78) * mm, "end": v(1.12, -10.69) * mm});
            skLineSegment(sketch, "E382", {"start": v(1.12, -10.69) * mm, "end": v(1.09, -10.64) * mm});
            skLineSegment(sketch, "E383", {"start": v(1.09, -10.64) * mm, "end": v(1.05, -10.6) * mm});
            skLineSegment(sketch, "E384", {"start": v(1.05, -10.6) * mm, "end": v(1, -10.55) * mm});
            skLineSegment(sketch, "E385", {"start": v(1, -10.55) * mm, "end": v(0.93, -10.5) * mm});
            skLineSegment(sketch, "E386", {"start": v(0.93, -10.5) * mm, "end": v(0, -10.5) * mm});
            skLineSegment(sketch, "E387", {"start": v(0, -10.5) * mm, "end": v(-0.93, -10.5) * mm});
            skLineSegment(sketch, "E388", {"start": v(-0.93, -10.5) * mm, "end": v(-1, -10.55) * mm});
            skLineSegment(sketch, "E389", {"start": v(-1, -10.55) * mm, "end": v(-1.05, -10.6) * mm});
            skLineSegment(sketch, "E390", {"start": v(-1.05, -10.6) * mm, "end": v(-1.09, -10.64) * mm});
            skLineSegment(sketch, "E391", {"start": v(-1.09, -10.64) * mm, "end": v(-1.12, -10.69) * mm});
            skLineSegment(sketch, "E392", {"start": v(-1.12, -10.69) * mm, "end": v(-1.17, -10.78) * mm});
            skLineSegment(sketch, "E393", {"start": v(-1.17, -10.78) * mm, "end": v(-1.22, -10.88) * mm});
            skLineSegment(sketch, "E394", {"start": v(-1.22, -10.88) * mm, "end": v(-1.25, -10.97) * mm});
            skLineSegment(sketch, "E395", {"start": v(-1.25, -10.97) * mm, "end": v(-1.28, -11.07) * mm});
            skLineSegment(sketch, "E396", {"start": v(-1.28, -11.07) * mm, "end": v(-1.32, -11.27) * mm});
            skLineSegment(sketch, "E397", {"start": v(-1.32, -11.27) * mm, "end": v(-1.38, -11.47) * mm});
            skLineSegment(sketch, "E398", {"start": v(-1.38, -11.47) * mm, "end": v(-1.45, -11.66) * mm});
            skLineSegment(sketch, "E399", {"start": v(-1.45, -11.66) * mm, "end": v(-1.54, -11.85) * mm});
            skLineSegment(sketch, "E400", {"start": v(-1.54, -11.85) * mm, "end": v(-1.64, -12.04) * mm});
            skLineSegment(sketch, "E401", {"start": v(-1.64, -12.04) * mm, "end": v(-1.76, -12.23) * mm});
            skLineSegment(sketch, "E402", {"start": v(-1.76, -12.23) * mm, "end": v(-1.88, -12.41) * mm});
            skLineSegment(sketch, "E403", {"start": v(-1.88, -12.41) * mm, "end": v(-2.01, -12.6) * mm});
            skLineSegment(sketch, "E404", {"start": v(-2.01, -12.6) * mm, "end": v(-2.15, -12.77) * mm});
            skLineSegment(sketch, "E405", {"start": v(-2.15, -12.77) * mm, "end": v(-2.3, -12.95) * mm});
            skLineSegment(sketch, "E406", {"start": v(-2.3, -12.95) * mm, "end": v(-2.46, -13.13) * mm});
            skLineSegment(sketch, "E407", {"start": v(-2.46, -13.13) * mm, "end": v(-2.58, -13.26) * mm});
            skLineSegment(sketch, "E408", {"start": v(-2.58, -13.26) * mm, "end": v(-4.4, -12.77) * mm});
            skLineSegment(sketch, "E409", {"start": v(-4.4, -12.77) * mm, "end": v(-4.43, -12.6) * mm});
            skLineSegment(sketch, "E410", {"start": v(-4.43, -12.6) * mm, "end": v(-4.48, -12.37) * mm});
            skLineSegment(sketch, "E411", {"start": v(-4.48, -12.37) * mm, "end": v(-4.52, -12.14) * mm});
            skLineSegment(sketch, "E412", {"start": v(-4.52, -12.14) * mm, "end": v(-4.56, -11.91) * mm});
            skLineSegment(sketch, "E413", {"start": v(-4.56, -11.91) * mm, "end": v(-4.58, -11.69) * mm});
            skLineSegment(sketch, "E414", {"start": v(-4.58, -11.69) * mm, "end": v(-4.6, -11.47) * mm});
            skLineSegment(sketch, "E415", {"start": v(-4.6, -11.47) * mm, "end": v(-4.6, -11.25) * mm});
            skLineSegment(sketch, "E416", {"start": v(-4.6, -11.25) * mm, "end": v(-4.59, -11.03) * mm});
            skLineSegment(sketch, "E417", {"start": v(-4.59, -11.03) * mm, "end": v(-4.57, -10.82) * mm});
            skLineSegment(sketch, "E418", {"start": v(-4.57, -10.82) * mm, "end": v(-4.54, -10.62) * mm});
            skLineSegment(sketch, "E419", {"start": v(-4.54, -10.62) * mm, "end": v(-4.5, -10.42) * mm});
            skLineSegment(sketch, "E420", {"start": v(-4.5, -10.42) * mm, "end": v(-4.43, -10.23) * mm});
            skLineSegment(sketch, "E421", {"start": v(-4.43, -10.23) * mm, "end": v(-4.4, -10.13) * mm});
            skLineSegment(sketch, "E422", {"start": v(-4.4, -10.13) * mm, "end": v(-4.38, -10.03) * mm});
            skLineSegment(sketch, "E423", {"start": v(-4.38, -10.03) * mm, "end": v(-4.37, -9.92) * mm});
            skLineSegment(sketch, "E424", {"start": v(-4.37, -9.92) * mm, "end": v(-4.37, -9.81) * mm});
            skLineSegment(sketch, "E425", {"start": v(-4.37, -9.81) * mm, "end": v(-4.38, -9.76) * mm});
            skLineSegment(sketch, "E426", {"start": v(-4.38, -9.76) * mm, "end": v(-4.39, -9.7) * mm});
            skLineSegment(sketch, "E427", {"start": v(-4.39, -9.7) * mm, "end": v(-4.4, -9.63) * mm});
            skLineSegment(sketch, "E428", {"start": v(-4.4, -9.63) * mm, "end": v(-4.44, -9.56) * mm});
            skLineSegment(sketch, "E429", {"start": v(-4.44, -9.56) * mm, "end": v(-5.25, -9.09) * mm});
            skLineSegment(sketch, "E430", {"start": v(-5.25, -9.09) * mm, "end": v(-6.06, -8.63) * mm});
            skLineSegment(sketch, "E431", {"start": v(-6.06, -8.63) * mm, "end": v(-6.14, -8.63) * mm});
            skLineSegment(sketch, "E432", {"start": v(-6.14, -8.63) * mm, "end": v(-6.2, -8.65) * mm});
            skLineSegment(sketch, "E433", {"start": v(-6.2, -8.65) * mm, "end": v(-6.26, -8.67) * mm});
            skLineSegment(sketch, "E434", {"start": v(-6.26, -8.67) * mm, "end": v(-6.31, -8.7) * mm});
            skLineSegment(sketch, "E435", {"start": v(-6.31, -8.7) * mm, "end": v(-6.4, -8.75) * mm});
            skLineSegment(sketch, "E436", {"start": v(-6.4, -8.75) * mm, "end": v(-6.5, -8.81) * mm});
            skLineSegment(sketch, "E437", {"start": v(-6.5, -8.81) * mm, "end": v(-6.57, -8.88) * mm});
            skLineSegment(sketch, "E438", {"start": v(-6.57, -8.88) * mm, "end": v(-6.64, -8.95) * mm});
            skLineSegment(sketch, "E439", {"start": v(-6.64, -8.95) * mm, "end": v(-6.78, -9.1) * mm});
            skLineSegment(sketch, "E440", {"start": v(-6.78, -9.1) * mm, "end": v(-6.92, -9.24) * mm});
            skLineSegment(sketch, "E441", {"start": v(-6.92, -9.24) * mm, "end": v(-7.09, -9.37) * mm});
            skLineSegment(sketch, "E442", {"start": v(-7.09, -9.37) * mm, "end": v(-7.26, -9.5) * mm});
            skLineSegment(sketch, "E443", {"start": v(-7.26, -9.5) * mm, "end": v(-7.44, -9.6) * mm});
            skLineSegment(sketch, "E444", {"start": v(-7.44, -9.6) * mm, "end": v(-7.63, -9.71) * mm});
            skLineSegment(sketch, "E445", {"start": v(-7.63, -9.71) * mm, "end": v(-7.83, -9.8) * mm});
            skLineSegment(sketch, "E446", {"start": v(-7.83, -9.8) * mm, "end": v(-8.04, -9.9) * mm});
            skLineSegment(sketch, "E447", {"start": v(-8.04, -9.9) * mm, "end": v(-8.25, -9.99) * mm});
            skLineSegment(sketch, "E448", {"start": v(-8.25, -9.99) * mm, "end": v(-8.47, -10.07) * mm});
            skLineSegment(sketch, "E449", {"start": v(-8.47, -10.07) * mm, "end": v(-8.7, -10.14) * mm});
            skLineSegment(sketch, "E450", {"start": v(-8.7, -10.14) * mm, "end": v(-8.87, -10.19) * mm});
            skLineSegment(sketch, "E451", {"start": v(-8.87, -10.19) * mm, "end": v(-10.2, -8.87) * mm});
            skLineSegment(sketch, "E452", {"start": v(-10.2, -8.87) * mm, "end": v(-10.14, -8.7) * mm});
            skLineSegment(sketch, "E453", {"start": v(-10.14, -8.7) * mm, "end": v(-10.07, -8.47) * mm});
            skLineSegment(sketch, "E454", {"start": v(-10.07, -8.47) * mm, "end": v(-9.99, -8.25) * mm});
            skLineSegment(sketch, "E455", {"start": v(-9.99, -8.25) * mm, "end": v(-9.9, -8.04) * mm});
            skLineSegment(sketch, "E456", {"start": v(-9.9, -8.04) * mm, "end": v(-9.8, -7.83) * mm});
            skLineSegment(sketch, "E457", {"start": v(-9.8, -7.83) * mm, "end": v(-9.71, -7.63) * mm});
            skLineSegment(sketch, "E458", {"start": v(-9.71, -7.63) * mm, "end": v(-9.6, -7.44) * mm});
            skLineSegment(sketch, "E459", {"start": v(-9.6, -7.44) * mm, "end": v(-9.5, -7.26) * mm});
            skLineSegment(sketch, "E460", {"start": v(-9.5, -7.26) * mm, "end": v(-9.37, -7.09) * mm});
            skLineSegment(sketch, "E461", {"start": v(-9.37, -7.09) * mm, "end": v(-9.24, -6.92) * mm});
            skLineSegment(sketch, "E462", {"start": v(-9.24, -6.92) * mm, "end": v(-9.1, -6.78) * mm});
            skLineSegment(sketch, "E463", {"start": v(-9.1, -6.78) * mm, "end": v(-8.95, -6.64) * mm});
            skLineSegment(sketch, "E464", {"start": v(-8.95, -6.64) * mm, "end": v(-8.88, -6.57) * mm});
            skLineSegment(sketch, "E465", {"start": v(-8.88, -6.57) * mm, "end": v(-8.81, -6.5) * mm});
            skLineSegment(sketch, "E466", {"start": v(-8.81, -6.5) * mm, "end": v(-8.75, -6.4) * mm});
            skLineSegment(sketch, "E467", {"start": v(-8.75, -6.4) * mm, "end": v(-8.7, -6.31) * mm});
            skLineSegment(sketch, "E468", {"start": v(-8.7, -6.31) * mm, "end": v(-8.67, -6.26) * mm});
            skLineSegment(sketch, "E469", {"start": v(-8.67, -6.26) * mm, "end": v(-8.65, -6.2) * mm});
            skLineSegment(sketch, "E470", {"start": v(-8.65, -6.2) * mm, "end": v(-8.63, -6.14) * mm});
            skLineSegment(sketch, "E471", {"start": v(-8.63, -6.14) * mm, "end": v(-8.63, -6.06) * mm});
            skLineSegment(sketch, "E472", {"start": v(-8.63, -6.06) * mm, "end": v(-9.09, -5.25) * mm});
            skLineSegment(sketch, "E473", {"start": v(-9.09, -5.25) * mm, "end": v(-9.56, -4.44) * mm});
            skLineSegment(sketch, "E474", {"start": v(-9.56, -4.44) * mm, "end": v(-9.63, -4.4) * mm});
            skLineSegment(sketch, "E475", {"start": v(-9.63, -4.4) * mm, "end": v(-9.7, -4.39) * mm});
            skLineSegment(sketch, "E476", {"start": v(-9.7, -4.39) * mm, "end": v(-9.76, -4.38) * mm});
            skLineSegment(sketch, "E477", {"start": v(-9.76, -4.38) * mm, "end": v(-9.81, -4.37) * mm});
            skLineSegment(sketch, "E478", {"start": v(-9.81, -4.37) * mm, "end": v(-9.92, -4.37) * mm});
            skLineSegment(sketch, "E479", {"start": v(-9.92, -4.37) * mm, "end": v(-10.03, -4.38) * mm});
            skLineSegment(sketch, "E480", {"start": v(-10.03, -4.38) * mm, "end": v(-10.13, -4.4) * mm});
            skLineSegment(sketch, "E481", {"start": v(-10.13, -4.4) * mm, "end": v(-10.23, -4.43) * mm});
            skLineSegment(sketch, "E482", {"start": v(-10.23, -4.43) * mm, "end": v(-10.42, -4.5) * mm});
            skLineSegment(sketch, "E483", {"start": v(-10.42, -4.5) * mm, "end": v(-10.62, -4.54) * mm});
            skLineSegment(sketch, "E484", {"start": v(-10.62, -4.54) * mm, "end": v(-10.82, -4.57) * mm});
            skLineSegment(sketch, "E485", {"start": v(-10.82, -4.57) * mm, "end": v(-11.03, -4.59) * mm});
            skLineSegment(sketch, "E486", {"start": v(-11.03, -4.59) * mm, "end": v(-11.25, -4.6) * mm});
            skLineSegment(sketch, "E487", {"start": v(-11.25, -4.6) * mm, "end": v(-11.47, -4.6) * mm});
            skLineSegment(sketch, "E488", {"start": v(-11.47, -4.6) * mm, "end": v(-11.69, -4.58) * mm});
            skLineSegment(sketch, "E489", {"start": v(-11.69, -4.58) * mm, "end": v(-11.91, -4.56) * mm});
            skLineSegment(sketch, "E490", {"start": v(-11.91, -4.56) * mm, "end": v(-12.14, -4.52) * mm});
            skLineSegment(sketch, "E491", {"start": v(-12.14, -4.52) * mm, "end": v(-12.37, -4.48) * mm});
            skLineSegment(sketch, "E492", {"start": v(-12.37, -4.48) * mm, "end": v(-12.6, -4.43) * mm});
            skLineSegment(sketch, "E493", {"start": v(-12.6, -4.43) * mm, "end": v(-12.77, -4.4) * mm});
            skLineSegment(sketch, "E494", {"start": v(-12.77, -4.4) * mm, "end": v(-13.26, -2.58) * mm});
            skLineSegment(sketch, "E495", {"start": v(-13.26, -2.58) * mm, "end": v(-13.13, -2.46) * mm});
            skLineSegment(sketch, "E496", {"start": v(-13.13, -2.46) * mm, "end": v(-12.95, -2.3) * mm});
            skLineSegment(sketch, "E497", {"start": v(-12.95, -2.3) * mm, "end": v(-12.77, -2.15) * mm});
            skLineSegment(sketch, "E498", {"start": v(-12.77, -2.15) * mm, "end": v(-12.6, -2.01) * mm});
            skLineSegment(sketch, "E499", {"start": v(-12.6, -2.01) * mm, "end": v(-12.41, -1.88) * mm});
            skLineSegment(sketch, "E500", {"start": v(-12.41, -1.88) * mm, "end": v(-12.23, -1.76) * mm});
            skLineSegment(sketch, "E501", {"start": v(-12.23, -1.76) * mm, "end": v(-12.04, -1.64) * mm});
            skLineSegment(sketch, "E502", {"start": v(-12.04, -1.64) * mm, "end": v(-11.85, -1.54) * mm});
            skLineSegment(sketch, "E503", {"start": v(-11.85, -1.54) * mm, "end": v(-11.66, -1.45) * mm});
            skLineSegment(sketch, "E504", {"start": v(-11.66, -1.45) * mm, "end": v(-11.47, -1.38) * mm});
            skLineSegment(sketch, "E505", {"start": v(-11.47, -1.38) * mm, "end": v(-11.27, -1.32) * mm});
            skLineSegment(sketch, "E506", {"start": v(-11.27, -1.32) * mm, "end": v(-11.07, -1.28) * mm});
            skLineSegment(sketch, "E507", {"start": v(-11.07, -1.28) * mm, "end": v(-10.97, -1.25) * mm});
            skLineSegment(sketch, "E508", {"start": v(-10.97, -1.25) * mm, "end": v(-10.88, -1.22) * mm});
            skLineSegment(sketch, "E509", {"start": v(-10.88, -1.22) * mm, "end": v(-10.78, -1.17) * mm});
            skLineSegment(sketch, "E510", {"start": v(-10.78, -1.17) * mm, "end": v(-10.69, -1.12) * mm});
            skLineSegment(sketch, "E511", {"start": v(-10.69, -1.12) * mm, "end": v(-10.64, -1.09) * mm});
            skLineSegment(sketch, "E512", {"start": v(-10.64, -1.09) * mm, "end": v(-10.6, -1.05) * mm});
            skLineSegment(sketch, "E513", {"start": v(-10.6, -1.05) * mm, "end": v(-10.55, -1) * mm});
            skLineSegment(sketch, "E514", {"start": v(-10.55, -1) * mm, "end": v(-10.5, -0.93) * mm});
            skLineSegment(sketch, "E515", {"start": v(-10.5, -0.93) * mm, "end": v(-10.5, 0) * mm});
            skPoint(sketch, "E516", {"position": v(0, 0) * mm});
            skLineSegment(sketch, "E517", {"start": v(-10.5, -0.93) * mm, "end": v(10.5, 0.93) * mm, "construction": true});
            skLineSegment(sketch, "E518", {"start": v(13.26, -2.58) * mm, "end": v(-13.26, 2.58) * mm, "construction": true});
            skLineSegment(sketch, "E519", {"start": v(10.5, 0.93) * mm, "end": v(12.77, 4.4) * mm, "construction": true});
            skLineSegment(sketch, "E520", {"start": v(8.63, 6.14) * mm, "end": v(9.63, 4.4) * mm, "construction": true});
            skLineSegment(sketch, "E521", {"start": v(9.13, 5.27) * mm, "end": v(0, 0) * mm, "construction": true});
            skLineSegment(sketch, "E522", {"start": v(0, 0) * mm, "end": v(-9.09, -5.25) * mm, "construction": true});
            skLineSegment(sketch, "E523", {"start": v(-2.58, 13.26) * mm, "end": v(2.58, 13.26) * mm, "construction": true});
            skArc(sketch, "E524", {"start": v(-2.58, 13.26) * mm, "mid": v(0, 13.6) * mm, "end": v(2.58, 13.26) * mm});
            skLineSegment(sketch, "E525", {"start": v(0, 10.5) * mm, "end": v(0.03, 13.6) * mm, "construction": true});
            skSolve(sketch);
        }
        {
            var Q0;
            Q0=makeQuery(id+"F0.imprint","IMPRINT",FACE,{"disambiguationData":[TD([[makeQuery(id+"F0.imprint","IMPRINT",EDGE,{"derivedFrom":sQuery(id+"F0.wireOp",EDGE,"E0")}),-1.0]])]});
            extrude(context, id + "F1", {"entities" : qUnion([Q0]), "depth" : 3 * mm});
        }
        {
            var Q0;
            Q0=makeQuery(id+"F1.opExtrude","CAP_FACE",FACE,{"disambiguationData":[OSD([sQuery(id+"F0.wireOp",EDGE,"E0"),sQuery(id+"F0.wireOp",EDGE,"E1"),sQuery(id+"F0.wireOp",EDGE,"E2"),sQuery(id+"F0.wireOp",EDGE,"E3"),sQuery(id+"F0.wireOp",EDGE,"E4"),sQuery(id+"F0.wireOp",EDGE,"E5"),sQuery(id+"F0.wireOp",EDGE,"E6"),sQuery(id+"F0.wireOp",EDGE,"E7"),sQuery(id+"F0.wireOp",EDGE,"E8"),sQuery(id+"F0.wireOp",EDGE,"E9"),sQuery(id+"F0.wireOp",EDGE,"E10"),sQuery(id+"F0.wireOp",EDGE,"E11"),sQuery(id+"F0.wireOp",EDGE,"E12"),sQuery(id+"F0.wireOp",EDGE,"E13"),sQuery(id+"F0.wireOp",EDGE,"E14"),sQuery(id+"F0.wireOp",EDGE,"E15"),sQuery(id+"F0.wireOp",EDGE,"E16"),sQuery(id+"F0.wireOp",EDGE,"E17"),sQuery(id+"F0.wireOp",EDGE,"E18"),sQuery(id+"F0.wireOp",EDGE,"E19"),sQuery(id+"F0.wireOp",EDGE,"E20"),sQuery(id+"F0.wireOp",EDGE,"E21"),sQuery(id+"F0.wireOp",EDGE,"E22"),sQuery(id+"F0.wireOp",EDGE,"E23"),sQuery(id+"F0.wireOp",EDGE,"E24"),sQuery(id+"F0.wireOp",EDGE,"E25"),sQuery(id+"F0.wireOp",EDGE,"E26"),sQuery(id+"F0.wireOp",EDGE,"E27"),sQuery(id+"F0.wireOp",EDGE,"E28"),sQuery(id+"F0.wireOp",EDGE,"E29"),sQuery(id+"F0.wireOp",EDGE,"E30"),sQuery(id+"F0.wireOp",EDGE,"E31"),sQuery(id+"F0.wireOp",EDGE,"E32"),sQuery(id+"F0.wireOp",EDGE,"E33"),sQuery(id+"F0.wireOp",EDGE,"E34"),sQuery(id+"F0.wireOp",EDGE,"E35"),sQuery(id+"F0.wireOp",EDGE,"E36"),sQuery(id+"F0.wireOp",EDGE,"E37"),sQuery(id+"F0.wireOp",EDGE,"E38"),sQuery(id+"F0.wireOp",EDGE,"E39"),sQuery(id+"F0.wireOp",EDGE,"E40"),sQuery(id+"F0.wireOp",EDGE,"E41"),sQuery(id+"F0.wireOp",EDGE,"E42"),sQuery(id+"F0.wireOp",EDGE,"E43"),sQuery(id+"F0.wireOp",EDGE,"E44"),sQuery(id+"F0.wireOp",EDGE,"E45"),sQuery(id+"F0.wireOp",EDGE,"E46"),sQuery(id+"F0.wireOp",EDGE,"E47"),sQuery(id+"F0.wireOp",EDGE,"E48"),sQuery(id+"F0.wireOp",EDGE,"E49"),sQuery(id+"F0.wireOp",EDGE,"E50"),sQuery(id+"F0.wireOp",EDGE,"E51"),sQuery(id+"F0.wireOp",EDGE,"E52"),sQuery(id+"F0.wireOp",EDGE,"E53"),sQuery(id+"F0.wireOp",EDGE,"E54"),sQuery(id+"F0.wireOp",EDGE,"E55"),sQuery(id+"F0.wireOp",EDGE,"E56"),sQuery(id+"F0.wireOp",EDGE,"E57"),sQuery(id+"F0.wireOp",EDGE,"E58"),sQuery(id+"F0.wireOp",EDGE,"E59"),sQuery(id+"F0.wireOp",EDGE,"E60"),sQuery(id+"F0.wireOp",EDGE,"E61"),sQuery(id+"F0.wireOp",EDGE,"E62"),sQuery(id+"F0.wireOp",EDGE,"E63"),sQuery(id+"F0.wireOp",EDGE,"E64"),sQuery(id+"F0.wireOp",EDGE,"E65"),sQuery(id+"F0.wireOp",EDGE,"E66"),sQuery(id+"F0.wireOp",EDGE,"E67"),sQuery(id+"F0.wireOp",EDGE,"E68"),sQuery(id+"F0.wireOp",EDGE,"E69"),sQuery(id+"F0.wireOp",EDGE,"E70"),sQuery(id+"F0.wireOp",EDGE,"E71"),sQuery(id+"F0.wireOp",EDGE,"E72"),sQuery(id+"F0.wireOp",EDGE,"E73"),sQuery(id+"F0.wireOp",EDGE,"E74"),sQuery(id+"F0.wireOp",EDGE,"E75"),sQuery(id+"F0.wireOp",EDGE,"E76"),sQuery(id+"F0.wireOp",EDGE,"E77"),sQuery(id+"F0.wireOp",EDGE,"E78"),sQuery(id+"F0.wireOp",EDGE,"E79"),sQuery(id+"F0.wireOp",EDGE,"E80"),sQuery(id+"F0.wireOp",EDGE,"E81"),sQuery(id+"F0.wireOp",EDGE,"E82"),sQuery(id+"F0.wireOp",EDGE,"E83"),sQuery(id+"F0.wireOp",EDGE,"E84"),sQuery(id+"F0.wireOp",EDGE,"E85"),sQuery(id+"F0.wireOp",EDGE,"E86"),sQuery(id+"F0.wireOp",EDGE,"E87"),sQuery(id+"F0.wireOp",EDGE,"E88"),sQuery(id+"F0.wireOp",EDGE,"E89"),sQuery(id+"F0.wireOp",EDGE,"E90"),sQuery(id+"F0.wireOp",EDGE,"E91"),sQuery(id+"F0.wireOp",EDGE,"E92"),sQuery(id+"F0.wireOp",EDGE,"E93"),sQuery(id+"F0.wireOp",EDGE,"E94"),sQuery(id+"F0.wireOp",EDGE,"E95"),sQuery(id+"F0.wireOp",EDGE,"E96"),sQuery(id+"F0.wireOp",EDGE,"E97"),sQuery(id+"F0.wireOp",EDGE,"E98"),sQuery(id+"F0.wireOp",EDGE,"E99"),sQuery(id+"F0.wireOp",EDGE,"E100"),sQuery(id+"F0.wireOp",EDGE,"E101"),sQuery(id+"F0.wireOp",EDGE,"E102"),sQuery(id+"F0.wireOp",EDGE,"E103"),sQuery(id+"F0.wireOp",EDGE,"E104"),sQuery(id+"F0.wireOp",EDGE,"E105"),sQuery(id+"F0.wireOp",EDGE,"E106"),sQuery(id+"F0.wireOp",EDGE,"E107"),sQuery(id+"F0.wireOp",EDGE,"E108"),sQuery(id+"F0.wireOp",EDGE,"E109"),sQuery(id+"F0.wireOp",EDGE,"E110"),sQuery(id+"F0.wireOp",EDGE,"E111"),sQuery(id+"F0.wireOp",EDGE,"E112"),sQuery(id+"F0.wireOp",EDGE,"E113"),sQuery(id+"F0.wireOp",EDGE,"E114"),sQuery(id+"F0.wireOp",EDGE,"E115"),sQuery(id+"F0.wireOp",EDGE,"E116"),sQuery(id+"F0.wireOp",EDGE,"E117"),sQuery(id+"F0.wireOp",EDGE,"E118"),sQuery(id+"F0.wireOp",EDGE,"E119"),sQuery(id+"F0.wireOp",EDGE,"E120"),sQuery(id+"F0.wireOp",EDGE,"E121"),sQuery(id+"F0.wireOp",EDGE,"E122"),sQuery(id+"F0.wireOp",EDGE,"E123"),sQuery(id+"F0.wireOp",EDGE,"E124"),sQuery(id+"F0.wireOp",EDGE,"E125"),sQuery(id+"F0.wireOp",EDGE,"E126"),sQuery(id+"F0.wireOp",EDGE,"E127"),sQuery(id+"F0.wireOp",EDGE,"E128"),sQuery(id+"F0.wireOp",EDGE,"E129"),sQuery(id+"F0.wireOp",EDGE,"E130"),sQuery(id+"F0.wireOp",EDGE,"E131"),sQuery(id+"F0.wireOp",EDGE,"E132"),sQuery(id+"F0.wireOp",EDGE,"E133"),sQuery(id+"F0.wireOp",EDGE,"E134"),sQuery(id+"F0.wireOp",EDGE,"E135"),sQuery(id+"F0.wireOp",EDGE,"E136"),sQuery(id+"F0.wireOp",EDGE,"E137"),sQuery(id+"F0.wireOp",EDGE,"E138"),sQuery(id+"F0.wireOp",EDGE,"E139"),sQuery(id+"F0.wireOp",EDGE,"E140"),sQuery(id+"F0.wireOp",EDGE,"E141"),sQuery(id+"F0.wireOp",EDGE,"E142"),sQuery(id+"F0.wireOp",EDGE,"E143"),sQuery(id+"F0.wireOp",EDGE,"E144"),sQuery(id+"F0.wireOp",EDGE,"E145"),sQuery(id+"F0.wireOp",EDGE,"E146"),sQuery(id+"F0.wireOp",EDGE,"E147"),sQuery(id+"F0.wireOp",EDGE,"E148"),sQuery(id+"F0.wireOp",EDGE,"E149"),sQuery(id+"F0.wireOp",EDGE,"E150"),sQuery(id+"F0.wireOp",EDGE,"E151"),sQuery(id+"F0.wireOp",EDGE,"E152"),sQuery(id+"F0.wireOp",EDGE,"E153"),sQuery(id+"F0.wireOp",EDGE,"E154"),sQuery(id+"F0.wireOp",EDGE,"E155"),sQuery(id+"F0.wireOp",EDGE,"E156"),sQuery(id+"F0.wireOp",EDGE,"E157"),sQuery(id+"F0.wireOp",EDGE,"E158"),sQuery(id+"F0.wireOp",EDGE,"E159"),sQuery(id+"F0.wireOp",EDGE,"E160"),sQuery(id+"F0.wireOp",EDGE,"E161"),sQuery(id+"F0.wireOp",EDGE,"E162"),sQuery(id+"F0.wireOp",EDGE,"E163"),sQuery(id+"F0.wireOp",EDGE,"E164"),sQuery(id+"F0.wireOp",EDGE,"E165"),sQuery(id+"F0.wireOp",EDGE,"E166"),sQuery(id+"F0.wireOp",EDGE,"E167"),sQuery(id+"F0.wireOp",EDGE,"E168"),sQuery(id+"F0.wireOp",EDGE,"E169"),sQuery(id+"F0.wireOp",EDGE,"E170"),sQuery(id+"F0.wireOp",EDGE,"E171"),sQuery(id+"F0.wireOp",EDGE,"E172"),sQuery(id+"F0.wireOp",EDGE,"E173"),sQuery(id+"F0.wireOp",EDGE,"E174"),sQuery(id+"F0.wireOp",EDGE,"E175"),sQuery(id+"F0.wireOp",EDGE,"E176"),sQuery(id+"F0.wireOp",EDGE,"E177"),sQuery(id+"F0.wireOp",EDGE,"E178"),sQuery(id+"F0.wireOp",EDGE,"E179"),sQuery(id+"F0.wireOp",EDGE,"E180"),sQuery(id+"F0.wireOp",EDGE,"E181"),sQuery(id+"F0.wireOp",EDGE,"E182"),sQuery(id+"F0.wireOp",EDGE,"E183"),sQuery(id+"F0.wireOp",EDGE,"E184"),sQuery(id+"F0.wireOp",EDGE,"E185"),sQuery(id+"F0.wireOp",EDGE,"E186"),sQuery(id+"F0.wireOp",EDGE,"E187"),sQuery(id+"F0.wireOp",EDGE,"E188"),sQuery(id+"F0.wireOp",EDGE,"E189"),sQuery(id+"F0.wireOp",EDGE,"E190"),sQuery(id+"F0.wireOp",EDGE,"E191"),sQuery(id+"F0.wireOp",EDGE,"E192"),sQuery(id+"F0.wireOp",EDGE,"E193"),sQuery(id+"F0.wireOp",EDGE,"E194"),sQuery(id+"F0.wireOp",EDGE,"E195"),sQuery(id+"F0.wireOp",EDGE,"E196"),sQuery(id+"F0.wireOp",EDGE,"E197"),sQuery(id+"F0.wireOp",EDGE,"E198"),sQuery(id+"F0.wireOp",EDGE,"E199"),sQuery(id+"F0.wireOp",EDGE,"E200"),sQuery(id+"F0.wireOp",EDGE,"E201"),sQuery(id+"F0.wireOp",EDGE,"E202"),sQuery(id+"F0.wireOp",EDGE,"E203"),sQuery(id+"F0.wireOp",EDGE,"E204"),sQuery(id+"F0.wireOp",EDGE,"E205"),sQuery(id+"F0.wireOp",EDGE,"E206"),sQuery(id+"F0.wireOp",EDGE,"E207"),sQuery(id+"F0.wireOp",EDGE,"E208"),sQuery(id+"F0.wireOp",EDGE,"E209"),sQuery(id+"F0.wireOp",EDGE,"E210"),sQuery(id+"F0.wireOp",EDGE,"E211"),sQuery(id+"F0.wireOp",EDGE,"E212"),sQuery(id+"F0.wireOp",EDGE,"E213"),sQuery(id+"F0.wireOp",EDGE,"E214"),sQuery(id+"F0.wireOp",EDGE,"E215"),sQuery(id+"F0.wireOp",EDGE,"E216"),sQuery(id+"F0.wireOp",EDGE,"E217"),sQuery(id+"F0.wireOp",EDGE,"E218"),sQuery(id+"F0.wireOp",EDGE,"E219"),sQuery(id+"F0.wireOp",EDGE,"E220"),sQuery(id+"F0.wireOp",EDGE,"E221"),sQuery(id+"F0.wireOp",EDGE,"E222"),sQuery(id+"F0.wireOp",EDGE,"E223"),sQuery(id+"F0.wireOp",EDGE,"E224"),sQuery(id+"F0.wireOp",EDGE,"E225"),sQuery(id+"F0.wireOp",EDGE,"E226"),sQuery(id+"F0.wireOp",EDGE,"E227"),sQuery(id+"F0.wireOp",EDGE,"E228"),sQuery(id+"F0.wireOp",EDGE,"E229"),sQuery(id+"F0.wireOp",EDGE,"E230"),sQuery(id+"F0.wireOp",EDGE,"E231"),sQuery(id+"F0.wireOp",EDGE,"E232"),sQuery(id+"F0.wireOp",EDGE,"E233"),sQuery(id+"F0.wireOp",EDGE,"E234"),sQuery(id+"F0.wireOp",EDGE,"E235"),sQuery(id+"F0.wireOp",EDGE,"E236"),sQuery(id+"F0.wireOp",EDGE,"E237"),sQuery(id+"F0.wireOp",EDGE,"E238"),sQuery(id+"F0.wireOp",EDGE,"E239"),sQuery(id+"F0.wireOp",EDGE,"E240"),sQuery(id+"F0.wireOp",EDGE,"E241"),sQuery(id+"F0.wireOp",EDGE,"E242"),sQuery(id+"F0.wireOp",EDGE,"E243"),sQuery(id+"F0.wireOp",EDGE,"E244"),sQuery(id+"F0.wireOp",EDGE,"E245"),sQuery(id+"F0.wireOp",EDGE,"E246"),sQuery(id+"F0.wireOp",EDGE,"E247"),sQuery(id+"F0.wireOp",EDGE,"E248"),sQuery(id+"F0.wireOp",EDGE,"E249"),sQuery(id+"F0.wireOp",EDGE,"E250"),sQuery(id+"F0.wireOp",EDGE,"E251"),sQuery(id+"F0.wireOp",EDGE,"E252"),sQuery(id+"F0.wireOp",EDGE,"E253"),sQuery(id+"F0.wireOp",EDGE,"E254"),sQuery(id+"F0.wireOp",EDGE,"E255"),sQuery(id+"F0.wireOp",EDGE,"E256"),sQuery(id+"F0.wireOp",EDGE,"E257"),sQuery(id+"F0.wireOp",EDGE,"E258"),sQuery(id+"F0.wireOp",EDGE,"E259"),sQuery(id+"F0.wireOp",EDGE,"E260"),sQuery(id+"F0.wireOp",EDGE,"E261"),sQuery(id+"F0.wireOp",EDGE,"E262"),sQuery(id+"F0.wireOp",EDGE,"E263"),sQuery(id+"F0.wireOp",EDGE,"E264"),sQuery(id+"F0.wireOp",EDGE,"E265"),sQuery(id+"F0.wireOp",EDGE,"E266"),sQuery(id+"F0.wireOp",EDGE,"E267"),sQuery(id+"F0.wireOp",EDGE,"E268"),sQuery(id+"F0.wireOp",EDGE,"E269"),sQuery(id+"F0.wireOp",EDGE,"E270"),sQuery(id+"F0.wireOp",EDGE,"E271"),sQuery(id+"F0.wireOp",EDGE,"E272"),sQuery(id+"F0.wireOp",EDGE,"E273"),sQuery(id+"F0.wireOp",EDGE,"E274"),sQuery(id+"F0.wireOp",EDGE,"E275"),sQuery(id+"F0.wireOp",EDGE,"E276"),sQuery(id+"F0.wireOp",EDGE,"E277"),sQuery(id+"F0.wireOp",EDGE,"E278"),sQuery(id+"F0.wireOp",EDGE,"E279"),sQuery(id+"F0.wireOp",EDGE,"E280"),sQuery(id+"F0.wireOp",EDGE,"E281"),sQuery(id+"F0.wireOp",EDGE,"E282"),sQuery(id+"F0.wireOp",EDGE,"E283"),sQuery(id+"F0.wireOp",EDGE,"E284"),sQuery(id+"F0.wireOp",EDGE,"E285"),sQuery(id+"F0.wireOp",EDGE,"E286"),sQuery(id+"F0.wireOp",EDGE,"E287"),sQuery(id+"F0.wireOp",EDGE,"E288"),sQuery(id+"F0.wireOp",EDGE,"E289"),sQuery(id+"F0.wireOp",EDGE,"E290"),sQuery(id+"F0.wireOp",EDGE,"E291"),sQuery(id+"F0.wireOp",EDGE,"E292"),sQuery(id+"F0.wireOp",EDGE,"E293"),sQuery(id+"F0.wireOp",EDGE,"E294"),sQuery(id+"F0.wireOp",EDGE,"E295"),sQuery(id+"F0.wireOp",EDGE,"E296"),sQuery(id+"F0.wireOp",EDGE,"E297"),sQuery(id+"F0.wireOp",EDGE,"E298"),sQuery(id+"F0.wireOp",EDGE,"E299"),sQuery(id+"F0.wireOp",EDGE,"E300"),sQuery(id+"F0.wireOp",EDGE,"E301"),sQuery(id+"F0.wireOp",EDGE,"E302"),sQuery(id+"F0.wireOp",EDGE,"E303"),sQuery(id+"F0.wireOp",EDGE,"E304"),sQuery(id+"F0.wireOp",EDGE,"E305"),sQuery(id+"F0.wireOp",EDGE,"E306"),sQuery(id+"F0.wireOp",EDGE,"E307"),sQuery(id+"F0.wireOp",EDGE,"E308"),sQuery(id+"F0.wireOp",EDGE,"E309"),sQuery(id+"F0.wireOp",EDGE,"E310"),sQuery(id+"F0.wireOp",EDGE,"E311"),sQuery(id+"F0.wireOp",EDGE,"E312"),sQuery(id+"F0.wireOp",EDGE,"E313"),sQuery(id+"F0.wireOp",EDGE,"E314"),sQuery(id+"F0.wireOp",EDGE,"E315"),sQuery(id+"F0.wireOp",EDGE,"E316"),sQuery(id+"F0.wireOp",EDGE,"E317"),sQuery(id+"F0.wireOp",EDGE,"E318"),sQuery(id+"F0.wireOp",EDGE,"E319"),sQuery(id+"F0.wireOp",EDGE,"E320"),sQuery(id+"F0.wireOp",EDGE,"E321"),sQuery(id+"F0.wireOp",EDGE,"E322"),sQuery(id+"F0.wireOp",EDGE,"E323"),sQuery(id+"F0.wireOp",EDGE,"E324"),sQuery(id+"F0.wireOp",EDGE,"E325"),sQuery(id+"F0.wireOp",EDGE,"E326"),sQuery(id+"F0.wireOp",EDGE,"E327"),sQuery(id+"F0.wireOp",EDGE,"E328"),sQuery(id+"F0.wireOp",EDGE,"E329"),sQuery(id+"F0.wireOp",EDGE,"E330"),sQuery(id+"F0.wireOp",EDGE,"E331"),sQuery(id+"F0.wireOp",EDGE,"E332"),sQuery(id+"F0.wireOp",EDGE,"E333"),sQuery(id+"F0.wireOp",EDGE,"E334"),sQuery(id+"F0.wireOp",EDGE,"E335"),sQuery(id+"F0.wireOp",EDGE,"E336"),sQuery(id+"F0.wireOp",EDGE,"E337"),sQuery(id+"F0.wireOp",EDGE,"E338"),sQuery(id+"F0.wireOp",EDGE,"E339"),sQuery(id+"F0.wireOp",EDGE,"E340"),sQuery(id+"F0.wireOp",EDGE,"E341"),sQuery(id+"F0.wireOp",EDGE,"E342"),sQuery(id+"F0.wireOp",EDGE,"E343"),sQuery(id+"F0.wireOp",EDGE,"E344"),sQuery(id+"F0.wireOp",EDGE,"E345"),sQuery(id+"F0.wireOp",EDGE,"E346"),sQuery(id+"F0.wireOp",EDGE,"E347"),sQuery(id+"F0.wireOp",EDGE,"E348"),sQuery(id+"F0.wireOp",EDGE,"E349"),sQuery(id+"F0.wireOp",EDGE,"E350"),sQuery(id+"F0.wireOp",EDGE,"E351"),sQuery(id+"F0.wireOp",EDGE,"E352"),sQuery(id+"F0.wireOp",EDGE,"E353"),sQuery(id+"F0.wireOp",EDGE,"E354"),sQuery(id+"F0.wireOp",EDGE,"E355"),sQuery(id+"F0.wireOp",EDGE,"E356"),sQuery(id+"F0.wireOp",EDGE,"E357"),sQuery(id+"F0.wireOp",EDGE,"E358"),sQuery(id+"F0.wireOp",EDGE,"E359"),sQuery(id+"F0.wireOp",EDGE,"E360"),sQuery(id+"F0.wireOp",EDGE,"E361"),sQuery(id+"F0.wireOp",EDGE,"E362"),sQuery(id+"F0.wireOp",EDGE,"E363"),sQuery(id+"F0.wireOp",EDGE,"E364"),sQuery(id+"F0.wireOp",EDGE,"E365"),sQuery(id+"F0.wireOp",EDGE,"E366"),sQuery(id+"F0.wireOp",EDGE,"E367"),sQuery(id+"F0.wireOp",EDGE,"E368"),sQuery(id+"F0.wireOp",EDGE,"E369"),sQuery(id+"F0.wireOp",EDGE,"E370"),sQuery(id+"F0.wireOp",EDGE,"E371"),sQuery(id+"F0.wireOp",EDGE,"E372"),sQuery(id+"F0.wireOp",EDGE,"E373"),sQuery(id+"F0.wireOp",EDGE,"E374"),sQuery(id+"F0.wireOp",EDGE,"E375"),sQuery(id+"F0.wireOp",EDGE,"E376"),sQuery(id+"F0.wireOp",EDGE,"E377"),sQuery(id+"F0.wireOp",EDGE,"E378"),sQuery(id+"F0.wireOp",EDGE,"E379"),sQuery(id+"F0.wireOp",EDGE,"E380"),sQuery(id+"F0.wireOp",EDGE,"E381"),sQuery(id+"F0.wireOp",EDGE,"E382"),sQuery(id+"F0.wireOp",EDGE,"E383"),sQuery(id+"F0.wireOp",EDGE,"E384"),sQuery(id+"F0.wireOp",EDGE,"E385"),sQuery(id+"F0.wireOp",EDGE,"E386"),sQuery(id+"F0.wireOp",EDGE,"E387"),sQuery(id+"F0.wireOp",EDGE,"E388"),sQuery(id+"F0.wireOp",EDGE,"E389"),sQuery(id+"F0.wireOp",EDGE,"E390"),sQuery(id+"F0.wireOp",EDGE,"E391"),sQuery(id+"F0.wireOp",EDGE,"E392"),sQuery(id+"F0.wireOp",EDGE,"E393"),sQuery(id+"F0.wireOp",EDGE,"E394"),sQuery(id+"F0.wireOp",EDGE,"E395"),sQuery(id+"F0.wireOp",EDGE,"E396"),sQuery(id+"F0.wireOp",EDGE,"E397"),sQuery(id+"F0.wireOp",EDGE,"E398"),sQuery(id+"F0.wireOp",EDGE,"E399"),sQuery(id+"F0.wireOp",EDGE,"E400"),sQuery(id+"F0.wireOp",EDGE,"E401"),sQuery(id+"F0.wireOp",EDGE,"E402"),sQuery(id+"F0.wireOp",EDGE,"E403"),sQuery(id+"F0.wireOp",EDGE,"E404"),sQuery(id+"F0.wireOp",EDGE,"E405"),sQuery(id+"F0.wireOp",EDGE,"E406"),sQuery(id+"F0.wireOp",EDGE,"E407"),sQuery(id+"F0.wireOp",EDGE,"E408"),sQuery(id+"F0.wireOp",EDGE,"E409"),sQuery(id+"F0.wireOp",EDGE,"E410"),sQuery(id+"F0.wireOp",EDGE,"E411"),sQuery(id+"F0.wireOp",EDGE,"E412"),sQuery(id+"F0.wireOp",EDGE,"E413"),sQuery(id+"F0.wireOp",EDGE,"E414"),sQuery(id+"F0.wireOp",EDGE,"E415"),sQuery(id+"F0.wireOp",EDGE,"E416"),sQuery(id+"F0.wireOp",EDGE,"E417"),sQuery(id+"F0.wireOp",EDGE,"E418"),sQuery(id+"F0.wireOp",EDGE,"E419"),sQuery(id+"F0.wireOp",EDGE,"E420"),sQuery(id+"F0.wireOp",EDGE,"E421"),sQuery(id+"F0.wireOp",EDGE,"E422"),sQuery(id+"F0.wireOp",EDGE,"E423"),sQuery(id+"F0.wireOp",EDGE,"E424"),sQuery(id+"F0.wireOp",EDGE,"E425"),sQuery(id+"F0.wireOp",EDGE,"E426"),sQuery(id+"F0.wireOp",EDGE,"E427"),sQuery(id+"F0.wireOp",EDGE,"E428"),sQuery(id+"F0.wireOp",EDGE,"E429"),sQuery(id+"F0.wireOp",EDGE,"E430"),sQuery(id+"F0.wireOp",EDGE,"E431"),sQuery(id+"F0.wireOp",EDGE,"E432"),sQuery(id+"F0.wireOp",EDGE,"E433"),sQuery(id+"F0.wireOp",EDGE,"E434"),sQuery(id+"F0.wireOp",EDGE,"E435"),sQuery(id+"F0.wireOp",EDGE,"E436"),sQuery(id+"F0.wireOp",EDGE,"E437"),sQuery(id+"F0.wireOp",EDGE,"E438"),sQuery(id+"F0.wireOp",EDGE,"E439"),sQuery(id+"F0.wireOp",EDGE,"E440"),sQuery(id+"F0.wireOp",EDGE,"E441"),sQuery(id+"F0.wireOp",EDGE,"E442"),sQuery(id+"F0.wireOp",EDGE,"E443"),sQuery(id+"F0.wireOp",EDGE,"E444"),sQuery(id+"F0.wireOp",EDGE,"E445"),sQuery(id+"F0.wireOp",EDGE,"E446"),sQuery(id+"F0.wireOp",EDGE,"E447"),sQuery(id+"F0.wireOp",EDGE,"E448"),sQuery(id+"F0.wireOp",EDGE,"E449"),sQuery(id+"F0.wireOp",EDGE,"E450"),sQuery(id+"F0.wireOp",EDGE,"E451"),sQuery(id+"F0.wireOp",EDGE,"E452"),sQuery(id+"F0.wireOp",EDGE,"E453"),sQuery(id+"F0.wireOp",EDGE,"E454"),sQuery(id+"F0.wireOp",EDGE,"E455"),sQuery(id+"F0.wireOp",EDGE,"E456"),sQuery(id+"F0.wireOp",EDGE,"E457"),sQuery(id+"F0.wireOp",EDGE,"E458"),sQuery(id+"F0.wireOp",EDGE,"E459"),sQuery(id+"F0.wireOp",EDGE,"E460"),sQuery(id+"F0.wireOp",EDGE,"E461"),sQuery(id+"F0.wireOp",EDGE,"E462"),sQuery(id+"F0.wireOp",EDGE,"E463"),sQuery(id+"F0.wireOp",EDGE,"E464"),sQuery(id+"F0.wireOp",EDGE,"E465"),sQuery(id+"F0.wireOp",EDGE,"E466"),sQuery(id+"F0.wireOp",EDGE,"E467"),sQuery(id+"F0.wireOp",EDGE,"E468"),sQuery(id+"F0.wireOp",EDGE,"E469"),sQuery(id+"F0.wireOp",EDGE,"E470"),sQuery(id+"F0.wireOp",EDGE,"E471"),sQuery(id+"F0.wireOp",EDGE,"E472"),sQuery(id+"F0.wireOp",EDGE,"E473"),sQuery(id+"F0.wireOp",EDGE,"E474"),sQuery(id+"F0.wireOp",EDGE,"E475"),sQuery(id+"F0.wireOp",EDGE,"E476"),sQuery(id+"F0.wireOp",EDGE,"E477"),sQuery(id+"F0.wireOp",EDGE,"E478"),sQuery(id+"F0.wireOp",EDGE,"E479"),sQuery(id+"F0.wireOp",EDGE,"E480"),sQuery(id+"F0.wireOp",EDGE,"E481"),sQuery(id+"F0.wireOp",EDGE,"E482"),sQuery(id+"F0.wireOp",EDGE,"E483"),sQuery(id+"F0.wireOp",EDGE,"E484"),sQuery(id+"F0.wireOp",EDGE,"E485"),sQuery(id+"F0.wireOp",EDGE,"E486"),sQuery(id+"F0.wireOp",EDGE,"E487"),sQuery(id+"F0.wireOp",EDGE,"E488"),sQuery(id+"F0.wireOp",EDGE,"E489"),sQuery(id+"F0.wireOp",EDGE,"E490"),sQuery(id+"F0.wireOp",EDGE,"E491"),sQuery(id+"F0.wireOp",EDGE,"E492"),sQuery(id+"F0.wireOp",EDGE,"E493"),sQuery(id+"F0.wireOp",EDGE,"E494"),sQuery(id+"F0.wireOp",EDGE,"E495"),sQuery(id+"F0.wireOp",EDGE,"E496"),sQuery(id+"F0.wireOp",EDGE,"E497"),sQuery(id+"F0.wireOp",EDGE,"E498"),sQuery(id+"F0.wireOp",EDGE,"E499"),sQuery(id+"F0.wireOp",EDGE,"E500"),sQuery(id+"F0.wireOp",EDGE,"E501"),sQuery(id+"F0.wireOp",EDGE,"E502"),sQuery(id+"F0.wireOp",EDGE,"E503"),sQuery(id+"F0.wireOp",EDGE,"E504"),sQuery(id+"F0.wireOp",EDGE,"E505"),sQuery(id+"F0.wireOp",EDGE,"E506"),sQuery(id+"F0.wireOp",EDGE,"E507"),sQuery(id+"F0.wireOp",EDGE,"E508"),sQuery(id+"F0.wireOp",EDGE,"E509"),sQuery(id+"F0.wireOp",EDGE,"E510"),sQuery(id+"F0.wireOp",EDGE,"E511"),sQuery(id+"F0.wireOp",EDGE,"E512"),sQuery(id+"F0.wireOp",EDGE,"E513"),sQuery(id+"F0.wireOp",EDGE,"E514"),sQuery(id+"F0.wireOp",EDGE,"E515")])],"isStart":false});
            var sketch = newSketch(context, id + "F2", { "sketchPlane" : qUnion([Q0])});
            skCircle(sketch, "E526", {"center": v(0, 0) * mm, "radius": 1.5 * mm});
            skSolve(sketch);
        }
        {
            var Q0;
            Q0=makeQuery(id+"F2.imprint","IMPRINT",FACE,{"disambiguationData":[TD([[makeQuery(id+"F2.imprint","IMPRINT",EDGE,{"derivedFrom":sQuery(id+"F2.wireOp",EDGE,"E526")}),1.0]])]});
            extrude(context, id + "F3", {"entities" : qUnion([Q0]), "operationType" : NewBodyOperationType.REMOVE, "endBound" : BoundingType.THROUGH_ALL, "oppositeDirection" : true, "depth" : 25 * mm});
        }
    });
